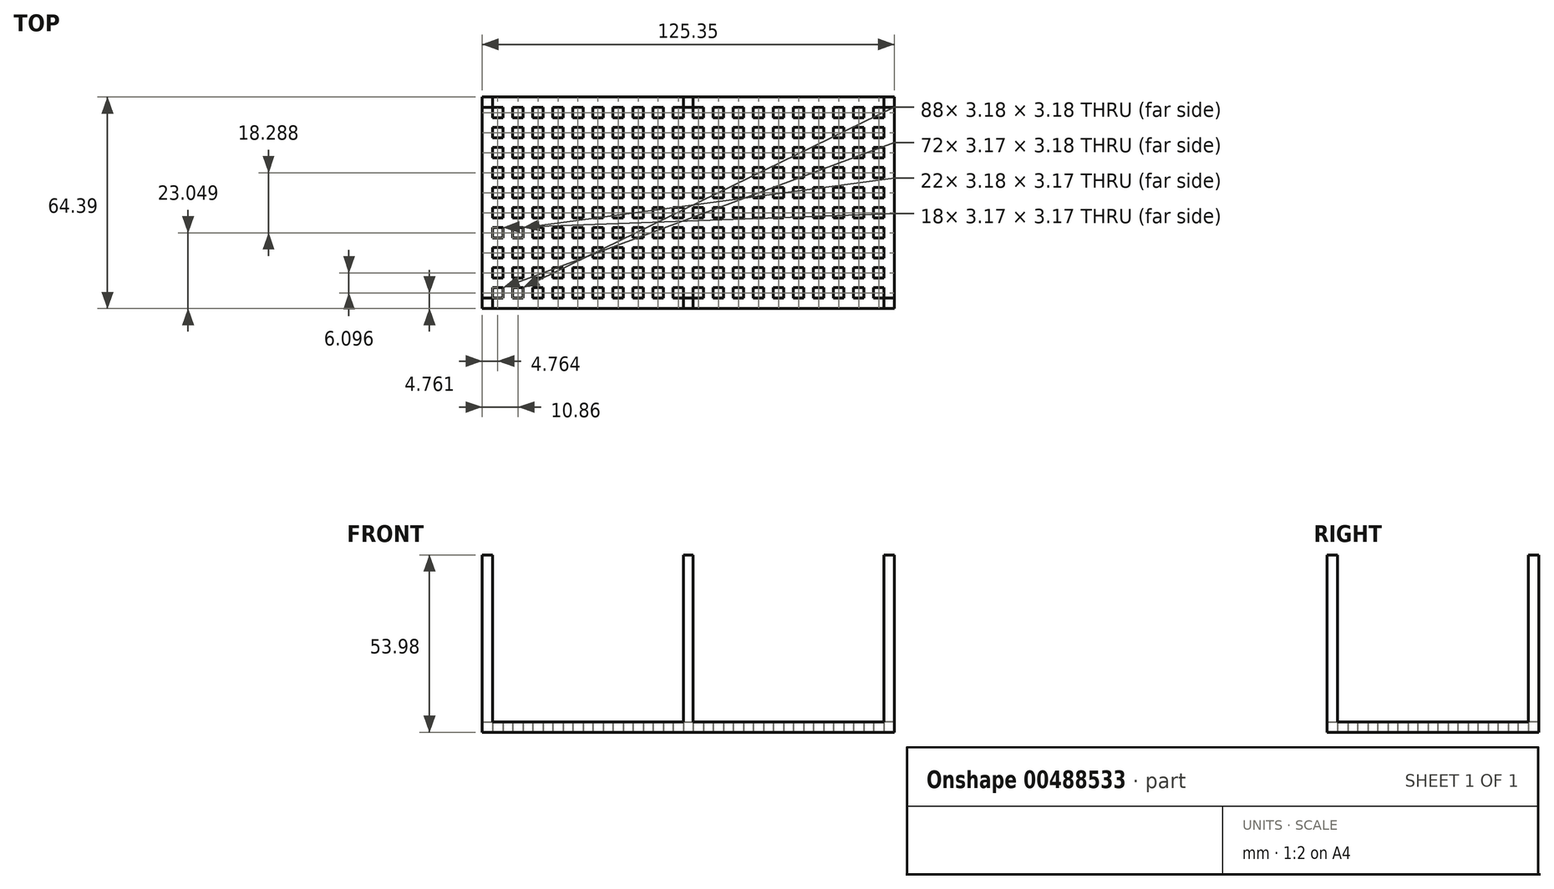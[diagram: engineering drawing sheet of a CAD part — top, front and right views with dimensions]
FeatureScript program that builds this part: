
annotation { "Feature Type Name" : "Feature", "Feature Type Description" : "" }
export const myFeature = defineFeature(function(context is Context, id is Id, definition is map)
    precondition{}
    {
        {
            var Q0;
            Q0=qCreatedBy(makeId("Top.planeOp"),FACE);
            var sketch = newSketch(context, id + "F0", { "sketchPlane" : qUnion([Q0])});
            skLineSegment(sketch, "E0.bottom", {"start": v(-61.85, 33.34) * mm, "end": v(63.5, 33.34) * mm});
            skLineSegment(sketch, "E0.top", {"start": v(-61.85, -31.05) * mm, "end": v(63.5, -31.05) * mm});
            skLineSegment(sketch, "E0.left", {"start": v(-61.85, 33.34) * mm, "end": v(-61.85, -31.05) * mm});
            skLineSegment(sketch, "E0.right", {"start": v(63.5, 33.34) * mm, "end": v(63.5, -31.05) * mm});
            skLineSegment(sketch, "E1.bottom", {"start": v(-58.67, 30.16) * mm, "end": v(-55.5, 30.16) * mm});
            skLineSegment(sketch, "E1.top", {"start": v(-58.67, 26.99) * mm, "end": v(-55.5, 26.99) * mm});
            skLineSegment(sketch, "E1.left", {"start": v(-58.67, 30.16) * mm, "end": v(-58.67, 26.99) * mm});
            skLineSegment(sketch, "E1.right", {"start": v(-55.5, 30.16) * mm, "end": v(-55.5, 26.99) * mm});
            skLineSegment(sketch, "E2.1.0.0", {"start": v(-52.58, 30.16) * mm, "end": v(-49.4, 30.16) * mm});
            skLineSegment(sketch, "E2.1.0.1", {"start": v(-52.58, 30.16) * mm, "end": v(-52.58, 26.99) * mm});
            skLineSegment(sketch, "E2.1.0.2", {"start": v(-52.58, 26.99) * mm, "end": v(-49.4, 26.99) * mm});
            skLineSegment(sketch, "E2.1.0.3", {"start": v(-49.4, 30.16) * mm, "end": v(-49.4, 26.99) * mm});
            skLineSegment(sketch, "E2.2.0.0", {"start": v(-46.48, 30.16) * mm, "end": v(-43.3, 30.16) * mm});
            skLineSegment(sketch, "E2.2.0.1", {"start": v(-46.48, 30.16) * mm, "end": v(-46.48, 26.99) * mm});
            skLineSegment(sketch, "E2.2.0.2", {"start": v(-46.48, 26.99) * mm, "end": v(-43.3, 26.99) * mm});
            skLineSegment(sketch, "E2.2.0.3", {"start": v(-43.3, 30.16) * mm, "end": v(-43.3, 26.99) * mm});
            skLineSegment(sketch, "E2.3.0.0", {"start": v(-40.39, 30.16) * mm, "end": v(-37.21, 30.16) * mm});
            skLineSegment(sketch, "E2.3.0.1", {"start": v(-40.39, 30.16) * mm, "end": v(-40.39, 26.99) * mm});
            skLineSegment(sketch, "E2.3.0.2", {"start": v(-40.39, 26.99) * mm, "end": v(-37.21, 26.99) * mm});
            skLineSegment(sketch, "E2.3.0.3", {"start": v(-37.21, 30.16) * mm, "end": v(-37.21, 26.99) * mm});
            skLineSegment(sketch, "E2.4.0.0", {"start": v(-34.29, 30.16) * mm, "end": v(-31.11, 30.16) * mm});
            skLineSegment(sketch, "E2.4.0.1", {"start": v(-34.29, 30.16) * mm, "end": v(-34.29, 26.99) * mm});
            skLineSegment(sketch, "E2.4.0.2", {"start": v(-34.29, 26.99) * mm, "end": v(-31.11, 26.99) * mm});
            skLineSegment(sketch, "E2.4.0.3", {"start": v(-31.11, 30.16) * mm, "end": v(-31.11, 26.99) * mm});
            skLineSegment(sketch, "E2.direction1", {"start": v(-58.67, 30.16) * mm, "end": v(-52.58, 30.16) * mm, "construction": true});
            skLineSegment(sketch, "E3.0.5.0", {"start": v(-28.2, 30.16) * mm, "end": v(-25.02, 30.16) * mm});
            skLineSegment(sketch, "E3.3.5.0", {"start": v(-28.2, 30.16) * mm, "end": v(-28.2, 26.99) * mm});
            skLineSegment(sketch, "E3.6.5.0", {"start": v(-28.2, 26.99) * mm, "end": v(-25.02, 26.99) * mm});
            skLineSegment(sketch, "E3.9.5.0", {"start": v(-25.02, 30.16) * mm, "end": v(-25.02, 26.99) * mm});
            skLineSegment(sketch, "E3.0.6.0", {"start": v(-22.1, 30.16) * mm, "end": v(-18.92, 30.16) * mm});
            skLineSegment(sketch, "E3.3.6.0", {"start": v(-22.1, 30.16) * mm, "end": v(-22.1, 26.99) * mm});
            skLineSegment(sketch, "E3.6.6.0", {"start": v(-22.1, 26.99) * mm, "end": v(-18.92, 26.99) * mm});
            skLineSegment(sketch, "E3.9.6.0", {"start": v(-18.92, 30.16) * mm, "end": v(-18.92, 26.99) * mm});
            skLineSegment(sketch, "E3.0.7.0", {"start": v(-16, 30.16) * mm, "end": v(-12.83, 30.16) * mm});
            skLineSegment(sketch, "E3.3.7.0", {"start": v(-16, 30.16) * mm, "end": v(-16, 26.99) * mm});
            skLineSegment(sketch, "E3.6.7.0", {"start": v(-16, 26.99) * mm, "end": v(-12.83, 26.99) * mm});
            skLineSegment(sketch, "E3.9.7.0", {"start": v(-12.83, 30.16) * mm, "end": v(-12.83, 26.99) * mm});
            skLineSegment(sketch, "E3.0.8.0", {"start": v(-9.9, 30.16) * mm, "end": v(-6.73, 30.16) * mm});
            skLineSegment(sketch, "E3.3.8.0", {"start": v(-9.9, 30.16) * mm, "end": v(-9.9, 26.99) * mm});
            skLineSegment(sketch, "E3.6.8.0", {"start": v(-9.9, 26.99) * mm, "end": v(-6.73, 26.99) * mm});
            skLineSegment(sketch, "E3.9.8.0", {"start": v(-6.73, 30.16) * mm, "end": v(-6.73, 26.99) * mm});
            skLineSegment(sketch, "E3.0.9.0", {"start": v(-3.8, 30.16) * mm, "end": v(-0.63, 30.16) * mm});
            skLineSegment(sketch, "E3.3.9.0", {"start": v(-3.8, 30.16) * mm, "end": v(-3.8, 26.99) * mm});
            skLineSegment(sketch, "E3.6.9.0", {"start": v(-3.8, 26.99) * mm, "end": v(-0.63, 26.99) * mm});
            skLineSegment(sketch, "E3.9.9.0", {"start": v(-0.63, 30.16) * mm, "end": v(-0.63, 26.99) * mm});
            skLineSegment(sketch, "E4.0.10.0", {"start": v(2.29, 30.16) * mm, "end": v(5.46, 30.16) * mm});
            skLineSegment(sketch, "E4.3.10.0", {"start": v(2.29, 30.16) * mm, "end": v(2.29, 26.99) * mm});
            skLineSegment(sketch, "E4.6.10.0", {"start": v(2.29, 26.99) * mm, "end": v(5.46, 26.99) * mm});
            skLineSegment(sketch, "E4.9.10.0", {"start": v(5.46, 30.16) * mm, "end": v(5.46, 26.99) * mm});
            skLineSegment(sketch, "E4.0.11.0", {"start": v(8.38, 30.16) * mm, "end": v(11.56, 30.16) * mm});
            skLineSegment(sketch, "E4.3.11.0", {"start": v(8.38, 30.16) * mm, "end": v(8.38, 26.99) * mm});
            skLineSegment(sketch, "E4.6.11.0", {"start": v(8.38, 26.99) * mm, "end": v(11.56, 26.99) * mm});
            skLineSegment(sketch, "E4.9.11.0", {"start": v(11.56, 30.16) * mm, "end": v(11.56, 26.99) * mm});
            skLineSegment(sketch, "E4.0.12.0", {"start": v(14.48, 30.16) * mm, "end": v(17.65, 30.16) * mm});
            skLineSegment(sketch, "E4.3.12.0", {"start": v(14.48, 30.16) * mm, "end": v(14.48, 26.99) * mm});
            skLineSegment(sketch, "E4.6.12.0", {"start": v(14.48, 26.99) * mm, "end": v(17.65, 26.99) * mm});
            skLineSegment(sketch, "E4.9.12.0", {"start": v(17.65, 30.16) * mm, "end": v(17.65, 26.99) * mm});
            skLineSegment(sketch, "E4.0.13.0", {"start": v(20.57, 30.16) * mm, "end": v(23.75, 30.16) * mm});
            skLineSegment(sketch, "E4.3.13.0", {"start": v(20.57, 30.16) * mm, "end": v(20.57, 26.99) * mm});
            skLineSegment(sketch, "E4.6.13.0", {"start": v(20.57, 26.99) * mm, "end": v(23.75, 26.99) * mm});
            skLineSegment(sketch, "E4.9.13.0", {"start": v(23.75, 30.16) * mm, "end": v(23.75, 26.99) * mm});
            skLineSegment(sketch, "E4.0.14.0", {"start": v(26.67, 30.16) * mm, "end": v(29.84, 30.16) * mm});
            skLineSegment(sketch, "E4.3.14.0", {"start": v(26.67, 30.16) * mm, "end": v(26.67, 26.99) * mm});
            skLineSegment(sketch, "E4.6.14.0", {"start": v(26.67, 26.99) * mm, "end": v(29.84, 26.99) * mm});
            skLineSegment(sketch, "E4.9.14.0", {"start": v(29.84, 30.16) * mm, "end": v(29.84, 26.99) * mm});
            skLineSegment(sketch, "E4.0.15.0", {"start": v(32.77, 30.16) * mm, "end": v(35.94, 30.16) * mm});
            skLineSegment(sketch, "E4.3.15.0", {"start": v(32.77, 30.16) * mm, "end": v(32.77, 26.99) * mm});
            skLineSegment(sketch, "E4.6.15.0", {"start": v(32.77, 26.99) * mm, "end": v(35.94, 26.99) * mm});
            skLineSegment(sketch, "E4.9.15.0", {"start": v(35.94, 30.16) * mm, "end": v(35.94, 26.99) * mm});
            skLineSegment(sketch, "E4.0.16.0", {"start": v(38.86, 30.16) * mm, "end": v(42.04, 30.16) * mm});
            skLineSegment(sketch, "E4.3.16.0", {"start": v(38.86, 30.16) * mm, "end": v(38.86, 26.99) * mm});
            skLineSegment(sketch, "E4.6.16.0", {"start": v(38.86, 26.99) * mm, "end": v(42.04, 26.99) * mm});
            skLineSegment(sketch, "E4.9.16.0", {"start": v(42.04, 30.16) * mm, "end": v(42.04, 26.99) * mm});
            skLineSegment(sketch, "E4.0.17.0", {"start": v(44.96, 30.16) * mm, "end": v(48.13, 30.16) * mm});
            skLineSegment(sketch, "E4.3.17.0", {"start": v(44.96, 30.16) * mm, "end": v(44.96, 26.99) * mm});
            skLineSegment(sketch, "E4.6.17.0", {"start": v(44.96, 26.99) * mm, "end": v(48.13, 26.99) * mm});
            skLineSegment(sketch, "E4.9.17.0", {"start": v(48.13, 30.16) * mm, "end": v(48.13, 26.99) * mm});
            skLineSegment(sketch, "E4.0.18.0", {"start": v(51.05, 30.16) * mm, "end": v(54.23, 30.16) * mm});
            skLineSegment(sketch, "E4.3.18.0", {"start": v(51.05, 30.16) * mm, "end": v(51.05, 26.99) * mm});
            skLineSegment(sketch, "E4.6.18.0", {"start": v(51.05, 26.99) * mm, "end": v(54.23, 26.99) * mm});
            skLineSegment(sketch, "E4.9.18.0", {"start": v(54.23, 30.16) * mm, "end": v(54.23, 26.99) * mm});
            skLineSegment(sketch, "E4.0.19.0", {"start": v(57.15, 30.16) * mm, "end": v(60.32, 30.16) * mm});
            skLineSegment(sketch, "E4.3.19.0", {"start": v(57.15, 30.16) * mm, "end": v(57.15, 26.99) * mm});
            skLineSegment(sketch, "E4.6.19.0", {"start": v(57.15, 26.99) * mm, "end": v(60.32, 26.99) * mm});
            skLineSegment(sketch, "E4.9.19.0", {"start": v(60.32, 30.16) * mm, "end": v(60.32, 26.99) * mm});
            skLineSegment(sketch, "E5.0.1.0", {"start": v(48.13, 24.07) * mm, "end": v(48.13, 20.9) * mm});
            skLineSegment(sketch, "E5.0.1.1", {"start": v(23.75, 24.07) * mm, "end": v(23.75, 20.9) * mm});
            skLineSegment(sketch, "E5.0.1.2", {"start": v(-0.63, 24.07) * mm, "end": v(-0.63, 20.9) * mm});
            skLineSegment(sketch, "E5.0.1.3", {"start": v(-25.02, 24.07) * mm, "end": v(-25.02, 20.9) * mm});
            skLineSegment(sketch, "E5.0.1.4", {"start": v(51.05, 24.07) * mm, "end": v(54.23, 24.07) * mm});
            skLineSegment(sketch, "E5.0.1.5", {"start": v(26.67, 24.07) * mm, "end": v(29.84, 24.07) * mm});
            skLineSegment(sketch, "E5.0.1.6", {"start": v(2.29, 24.07) * mm, "end": v(5.46, 24.07) * mm});
            skLineSegment(sketch, "E5.0.1.7", {"start": v(-22.1, 24.07) * mm, "end": v(-18.92, 24.07) * mm});
            skLineSegment(sketch, "E5.0.1.8", {"start": v(51.05, 24.07) * mm, "end": v(51.05, 20.9) * mm});
            skLineSegment(sketch, "E5.0.1.9", {"start": v(26.67, 24.07) * mm, "end": v(26.67, 20.9) * mm});
            skLineSegment(sketch, "E5.0.1.10", {"start": v(2.29, 24.07) * mm, "end": v(2.29, 20.9) * mm});
            skLineSegment(sketch, "E5.0.1.11", {"start": v(-22.1, 24.07) * mm, "end": v(-22.1, 20.9) * mm});
            skLineSegment(sketch, "E5.0.1.12", {"start": v(-43.3, 24.07) * mm, "end": v(-43.3, 20.9) * mm});
            skLineSegment(sketch, "E5.0.1.13", {"start": v(51.05, 20.9) * mm, "end": v(54.23, 20.9) * mm});
            skLineSegment(sketch, "E5.0.1.14", {"start": v(26.67, 20.9) * mm, "end": v(29.84, 20.9) * mm});
            skLineSegment(sketch, "E5.0.1.15", {"start": v(2.29, 20.9) * mm, "end": v(5.46, 20.9) * mm});
            skLineSegment(sketch, "E5.0.1.16", {"start": v(-22.1, 20.9) * mm, "end": v(-18.92, 20.9) * mm});
            skLineSegment(sketch, "E5.0.1.17", {"start": v(-40.39, 24.07) * mm, "end": v(-37.21, 24.07) * mm});
            skLineSegment(sketch, "E5.0.1.18", {"start": v(54.23, 24.07) * mm, "end": v(54.23, 20.9) * mm});
            skLineSegment(sketch, "E5.0.1.19", {"start": v(29.84, 24.07) * mm, "end": v(29.84, 20.9) * mm});
            skLineSegment(sketch, "E5.0.1.20", {"start": v(5.46, 24.07) * mm, "end": v(5.46, 20.9) * mm});
            skLineSegment(sketch, "E5.0.1.21", {"start": v(-18.92, 24.07) * mm, "end": v(-18.92, 20.9) * mm});
            skLineSegment(sketch, "E5.0.1.22", {"start": v(-40.39, 24.07) * mm, "end": v(-40.39, 20.9) * mm});
            skLineSegment(sketch, "E5.0.1.23", {"start": v(57.15, 24.07) * mm, "end": v(60.32, 24.07) * mm});
            skLineSegment(sketch, "E5.0.1.24", {"start": v(32.77, 24.07) * mm, "end": v(35.94, 24.07) * mm});
            skLineSegment(sketch, "E5.0.1.25", {"start": v(8.38, 24.07) * mm, "end": v(11.56, 24.07) * mm});
            skLineSegment(sketch, "E5.0.1.26", {"start": v(-16, 24.07) * mm, "end": v(-12.83, 24.07) * mm});
            skLineSegment(sketch, "E5.0.1.27", {"start": v(-40.39, 20.9) * mm, "end": v(-37.21, 20.9) * mm});
            skLineSegment(sketch, "E5.0.1.28", {"start": v(57.15, 24.07) * mm, "end": v(57.15, 20.9) * mm});
            skLineSegment(sketch, "E5.0.1.29", {"start": v(32.77, 24.07) * mm, "end": v(32.77, 20.9) * mm});
            skLineSegment(sketch, "E5.0.1.30", {"start": v(8.38, 24.07) * mm, "end": v(8.38, 20.9) * mm});
            skLineSegment(sketch, "E5.0.1.31", {"start": v(-16, 24.07) * mm, "end": v(-16, 20.9) * mm});
            skLineSegment(sketch, "E5.0.1.32", {"start": v(-37.21, 24.07) * mm, "end": v(-37.21, 20.9) * mm});
            skLineSegment(sketch, "E5.0.1.33", {"start": v(57.15, 20.9) * mm, "end": v(60.32, 20.9) * mm});
            skLineSegment(sketch, "E5.0.1.34", {"start": v(32.77, 20.9) * mm, "end": v(35.94, 20.9) * mm});
            skLineSegment(sketch, "E5.0.1.35", {"start": v(8.38, 20.9) * mm, "end": v(11.56, 20.9) * mm});
            skLineSegment(sketch, "E5.0.1.36", {"start": v(-16, 20.9) * mm, "end": v(-12.83, 20.9) * mm});
            skLineSegment(sketch, "E5.0.1.37", {"start": v(-34.29, 24.07) * mm, "end": v(-31.11, 24.07) * mm});
            skLineSegment(sketch, "E5.0.1.38", {"start": v(60.32, 24.07) * mm, "end": v(60.32, 20.9) * mm});
            skLineSegment(sketch, "E5.0.1.39", {"start": v(35.94, 24.07) * mm, "end": v(35.94, 20.9) * mm});
            skLineSegment(sketch, "E5.0.1.40", {"start": v(11.56, 24.07) * mm, "end": v(11.56, 20.9) * mm});
            skLineSegment(sketch, "E5.0.1.41", {"start": v(-12.83, 24.07) * mm, "end": v(-12.83, 20.9) * mm});
            skLineSegment(sketch, "E5.0.1.42", {"start": v(-34.29, 24.07) * mm, "end": v(-34.29, 20.9) * mm});
            skLineSegment(sketch, "E5.0.1.43", {"start": v(38.86, 24.07) * mm, "end": v(42.04, 24.07) * mm});
            skLineSegment(sketch, "E5.0.1.44", {"start": v(14.48, 24.07) * mm, "end": v(17.65, 24.07) * mm});
            skLineSegment(sketch, "E5.0.1.45", {"start": v(-9.9, 24.07) * mm, "end": v(-6.73, 24.07) * mm});
            skLineSegment(sketch, "E5.0.1.46", {"start": v(14.48, 24.07) * mm, "end": v(14.48, 20.9) * mm});
            skLineSegment(sketch, "E5.0.1.47", {"start": v(-9.9, 24.07) * mm, "end": v(-9.9, 20.9) * mm});
            skLineSegment(sketch, "E5.0.1.48", {"start": v(-34.29, 20.9) * mm, "end": v(-31.11, 20.9) * mm});
            skLineSegment(sketch, "E5.0.1.49", {"start": v(38.86, 24.07) * mm, "end": v(38.86, 20.9) * mm});
            skLineSegment(sketch, "E5.0.1.50", {"start": v(14.48, 20.9) * mm, "end": v(17.65, 20.9) * mm});
            skLineSegment(sketch, "E5.0.1.51", {"start": v(-9.9, 20.9) * mm, "end": v(-6.73, 20.9) * mm});
            skLineSegment(sketch, "E5.0.1.52", {"start": v(-31.11, 24.07) * mm, "end": v(-31.11, 20.9) * mm});
            skLineSegment(sketch, "E5.0.1.53", {"start": v(38.86, 20.9) * mm, "end": v(42.04, 20.9) * mm});
            skLineSegment(sketch, "E5.0.1.54", {"start": v(17.65, 24.07) * mm, "end": v(17.65, 20.9) * mm});
            skLineSegment(sketch, "E5.0.1.55", {"start": v(-6.73, 24.07) * mm, "end": v(-6.73, 20.9) * mm});
            skLineSegment(sketch, "E5.0.1.56", {"start": v(-58.67, 24.07) * mm, "end": v(-52.58, 24.07) * mm, "construction": true});
            skLineSegment(sketch, "E5.0.1.57", {"start": v(42.04, 24.07) * mm, "end": v(42.04, 20.9) * mm});
            skLineSegment(sketch, "E5.0.1.58", {"start": v(20.57, 24.07) * mm, "end": v(23.75, 24.07) * mm});
            skLineSegment(sketch, "E5.0.1.59", {"start": v(-3.8, 24.07) * mm, "end": v(-0.63, 24.07) * mm});
            skLineSegment(sketch, "E5.0.1.60", {"start": v(-28.2, 24.07) * mm, "end": v(-25.02, 24.07) * mm});
            skLineSegment(sketch, "E5.0.1.61", {"start": v(44.96, 24.07) * mm, "end": v(48.13, 24.07) * mm});
            skLineSegment(sketch, "E5.0.1.62", {"start": v(20.57, 24.07) * mm, "end": v(20.57, 20.9) * mm});
            skLineSegment(sketch, "E5.0.1.63", {"start": v(-3.8, 24.07) * mm, "end": v(-3.8, 20.9) * mm});
            skLineSegment(sketch, "E5.0.1.64", {"start": v(-28.2, 24.07) * mm, "end": v(-28.2, 20.9) * mm});
            skLineSegment(sketch, "E5.0.1.65", {"start": v(44.96, 24.07) * mm, "end": v(44.96, 20.9) * mm});
            skLineSegment(sketch, "E5.0.1.66", {"start": v(20.57, 20.9) * mm, "end": v(23.75, 20.9) * mm});
            skLineSegment(sketch, "E5.0.1.67", {"start": v(-3.8, 20.9) * mm, "end": v(-0.63, 20.9) * mm});
            skLineSegment(sketch, "E5.0.1.68", {"start": v(-28.2, 20.9) * mm, "end": v(-25.02, 20.9) * mm});
            skLineSegment(sketch, "E5.0.1.69", {"start": v(44.96, 20.9) * mm, "end": v(48.13, 20.9) * mm});
            skLineSegment(sketch, "E5.0.1.70", {"start": v(-46.48, 24.07) * mm, "end": v(-43.3, 24.07) * mm});
            skLineSegment(sketch, "E5.0.1.71", {"start": v(-46.48, 24.07) * mm, "end": v(-46.48, 20.9) * mm});
            skLineSegment(sketch, "E5.0.1.72", {"start": v(-46.48, 20.9) * mm, "end": v(-43.3, 20.9) * mm});
            skLineSegment(sketch, "E5.0.1.73", {"start": v(-58.67, 20.9) * mm, "end": v(-55.5, 20.9) * mm});
            skLineSegment(sketch, "E5.0.1.74", {"start": v(-58.67, 24.07) * mm, "end": v(-58.67, 20.9) * mm});
            skLineSegment(sketch, "E5.0.1.75", {"start": v(-55.5, 24.07) * mm, "end": v(-55.5, 20.9) * mm});
            skLineSegment(sketch, "E5.0.1.76", {"start": v(-52.58, 24.07) * mm, "end": v(-49.4, 24.07) * mm});
            skLineSegment(sketch, "E5.0.1.77", {"start": v(-52.58, 24.07) * mm, "end": v(-52.58, 20.9) * mm});
            skLineSegment(sketch, "E5.0.1.78", {"start": v(-52.58, 20.9) * mm, "end": v(-49.4, 20.9) * mm});
            skLineSegment(sketch, "E5.0.1.79", {"start": v(-49.4, 24.07) * mm, "end": v(-49.4, 20.9) * mm});
            skLineSegment(sketch, "E5.0.1.80", {"start": v(-58.67, 24.07) * mm, "end": v(-55.5, 24.07) * mm});
            skLineSegment(sketch, "E5.0.2.0", {"start": v(48.13, 17.97) * mm, "end": v(48.13, 14.8) * mm});
            skLineSegment(sketch, "E5.0.2.1", {"start": v(23.75, 17.97) * mm, "end": v(23.75, 14.8) * mm});
            skLineSegment(sketch, "E5.0.2.2", {"start": v(-0.63, 17.97) * mm, "end": v(-0.63, 14.8) * mm});
            skLineSegment(sketch, "E5.0.2.3", {"start": v(-25.02, 17.97) * mm, "end": v(-25.02, 14.8) * mm});
            skLineSegment(sketch, "E5.0.2.4", {"start": v(51.05, 17.97) * mm, "end": v(54.23, 17.97) * mm});
            skLineSegment(sketch, "E5.0.2.5", {"start": v(26.67, 17.97) * mm, "end": v(29.84, 17.97) * mm});
            skLineSegment(sketch, "E5.0.2.6", {"start": v(2.29, 17.97) * mm, "end": v(5.46, 17.97) * mm});
            skLineSegment(sketch, "E5.0.2.7", {"start": v(-22.1, 17.97) * mm, "end": v(-18.92, 17.97) * mm});
            skLineSegment(sketch, "E5.0.2.8", {"start": v(51.05, 17.97) * mm, "end": v(51.05, 14.8) * mm});
            skLineSegment(sketch, "E5.0.2.9", {"start": v(26.67, 17.97) * mm, "end": v(26.67, 14.8) * mm});
            skLineSegment(sketch, "E5.0.2.10", {"start": v(2.29, 17.97) * mm, "end": v(2.29, 14.8) * mm});
            skLineSegment(sketch, "E5.0.2.11", {"start": v(-22.1, 17.97) * mm, "end": v(-22.1, 14.8) * mm});
            skLineSegment(sketch, "E5.0.2.12", {"start": v(-43.3, 17.97) * mm, "end": v(-43.3, 14.8) * mm});
            skLineSegment(sketch, "E5.0.2.13", {"start": v(51.05, 14.8) * mm, "end": v(54.23, 14.8) * mm});
            skLineSegment(sketch, "E5.0.2.14", {"start": v(26.67, 14.8) * mm, "end": v(29.84, 14.8) * mm});
            skLineSegment(sketch, "E5.0.2.15", {"start": v(2.29, 14.8) * mm, "end": v(5.46, 14.8) * mm});
            skLineSegment(sketch, "E5.0.2.16", {"start": v(-22.1, 14.8) * mm, "end": v(-18.92, 14.8) * mm});
            skLineSegment(sketch, "E5.0.2.17", {"start": v(-40.39, 17.97) * mm, "end": v(-37.21, 17.97) * mm});
            skLineSegment(sketch, "E5.0.2.18", {"start": v(54.23, 17.97) * mm, "end": v(54.23, 14.8) * mm});
            skLineSegment(sketch, "E5.0.2.19", {"start": v(29.84, 17.97) * mm, "end": v(29.84, 14.8) * mm});
            skLineSegment(sketch, "E5.0.2.20", {"start": v(5.46, 17.97) * mm, "end": v(5.46, 14.8) * mm});
            skLineSegment(sketch, "E5.0.2.21", {"start": v(-18.92, 17.97) * mm, "end": v(-18.92, 14.8) * mm});
            skLineSegment(sketch, "E5.0.2.22", {"start": v(-40.39, 17.97) * mm, "end": v(-40.39, 14.8) * mm});
            skLineSegment(sketch, "E5.0.2.23", {"start": v(57.15, 17.97) * mm, "end": v(60.32, 17.97) * mm});
            skLineSegment(sketch, "E5.0.2.24", {"start": v(32.77, 17.97) * mm, "end": v(35.94, 17.97) * mm});
            skLineSegment(sketch, "E5.0.2.25", {"start": v(8.38, 17.97) * mm, "end": v(11.56, 17.97) * mm});
            skLineSegment(sketch, "E5.0.2.26", {"start": v(-16, 17.97) * mm, "end": v(-12.83, 17.97) * mm});
            skLineSegment(sketch, "E5.0.2.27", {"start": v(-40.39, 14.8) * mm, "end": v(-37.21, 14.8) * mm});
            skLineSegment(sketch, "E5.0.2.28", {"start": v(57.15, 17.97) * mm, "end": v(57.15, 14.8) * mm});
            skLineSegment(sketch, "E5.0.2.29", {"start": v(32.77, 17.97) * mm, "end": v(32.77, 14.8) * mm});
            skLineSegment(sketch, "E5.0.2.30", {"start": v(8.38, 17.97) * mm, "end": v(8.38, 14.8) * mm});
            skLineSegment(sketch, "E5.0.2.31", {"start": v(-16, 17.97) * mm, "end": v(-16, 14.8) * mm});
            skLineSegment(sketch, "E5.0.2.32", {"start": v(-37.21, 17.97) * mm, "end": v(-37.21, 14.8) * mm});
            skLineSegment(sketch, "E5.0.2.33", {"start": v(57.15, 14.8) * mm, "end": v(60.32, 14.8) * mm});
            skLineSegment(sketch, "E5.0.2.34", {"start": v(32.77, 14.8) * mm, "end": v(35.94, 14.8) * mm});
            skLineSegment(sketch, "E5.0.2.35", {"start": v(8.38, 14.8) * mm, "end": v(11.56, 14.8) * mm});
            skLineSegment(sketch, "E5.0.2.36", {"start": v(-16, 14.8) * mm, "end": v(-12.83, 14.8) * mm});
            skLineSegment(sketch, "E5.0.2.37", {"start": v(-34.29, 17.97) * mm, "end": v(-31.11, 17.97) * mm});
            skLineSegment(sketch, "E5.0.2.38", {"start": v(60.32, 17.97) * mm, "end": v(60.32, 14.8) * mm});
            skLineSegment(sketch, "E5.0.2.39", {"start": v(35.94, 17.97) * mm, "end": v(35.94, 14.8) * mm});
            skLineSegment(sketch, "E5.0.2.40", {"start": v(11.56, 17.97) * mm, "end": v(11.56, 14.8) * mm});
            skLineSegment(sketch, "E5.0.2.41", {"start": v(-12.83, 17.97) * mm, "end": v(-12.83, 14.8) * mm});
            skLineSegment(sketch, "E5.0.2.42", {"start": v(-34.29, 17.97) * mm, "end": v(-34.29, 14.8) * mm});
            skLineSegment(sketch, "E5.0.2.43", {"start": v(38.86, 17.97) * mm, "end": v(42.04, 17.97) * mm});
            skLineSegment(sketch, "E5.0.2.44", {"start": v(14.48, 17.97) * mm, "end": v(17.65, 17.97) * mm});
            skLineSegment(sketch, "E5.0.2.45", {"start": v(-9.9, 17.97) * mm, "end": v(-6.73, 17.97) * mm});
            skLineSegment(sketch, "E5.0.2.46", {"start": v(14.48, 17.97) * mm, "end": v(14.48, 14.8) * mm});
            skLineSegment(sketch, "E5.0.2.47", {"start": v(-9.9, 17.97) * mm, "end": v(-9.9, 14.8) * mm});
            skLineSegment(sketch, "E5.0.2.48", {"start": v(-34.29, 14.8) * mm, "end": v(-31.11, 14.8) * mm});
            skLineSegment(sketch, "E5.0.2.49", {"start": v(38.86, 17.97) * mm, "end": v(38.86, 14.8) * mm});
            skLineSegment(sketch, "E5.0.2.50", {"start": v(14.48, 14.8) * mm, "end": v(17.65, 14.8) * mm});
            skLineSegment(sketch, "E5.0.2.51", {"start": v(-9.9, 14.8) * mm, "end": v(-6.73, 14.8) * mm});
            skLineSegment(sketch, "E5.0.2.52", {"start": v(-31.11, 17.97) * mm, "end": v(-31.11, 14.8) * mm});
            skLineSegment(sketch, "E5.0.2.53", {"start": v(38.86, 14.8) * mm, "end": v(42.04, 14.8) * mm});
            skLineSegment(sketch, "E5.0.2.54", {"start": v(17.65, 17.97) * mm, "end": v(17.65, 14.8) * mm});
            skLineSegment(sketch, "E5.0.2.55", {"start": v(-6.73, 17.97) * mm, "end": v(-6.73, 14.8) * mm});
            skLineSegment(sketch, "E5.0.2.56", {"start": v(-58.67, 17.97) * mm, "end": v(-52.58, 17.97) * mm, "construction": true});
            skLineSegment(sketch, "E5.0.2.57", {"start": v(42.04, 17.97) * mm, "end": v(42.04, 14.8) * mm});
            skLineSegment(sketch, "E5.0.2.58", {"start": v(20.57, 17.97) * mm, "end": v(23.75, 17.97) * mm});
            skLineSegment(sketch, "E5.0.2.59", {"start": v(-3.8, 17.97) * mm, "end": v(-0.63, 17.97) * mm});
            skLineSegment(sketch, "E5.0.2.60", {"start": v(-28.2, 17.97) * mm, "end": v(-25.02, 17.97) * mm});
            skLineSegment(sketch, "E5.0.2.61", {"start": v(44.96, 17.97) * mm, "end": v(48.13, 17.97) * mm});
            skLineSegment(sketch, "E5.0.2.62", {"start": v(20.57, 17.97) * mm, "end": v(20.57, 14.8) * mm});
            skLineSegment(sketch, "E5.0.2.63", {"start": v(-3.8, 17.97) * mm, "end": v(-3.8, 14.8) * mm});
            skLineSegment(sketch, "E5.0.2.64", {"start": v(-28.2, 17.97) * mm, "end": v(-28.2, 14.8) * mm});
            skLineSegment(sketch, "E5.0.2.65", {"start": v(44.96, 17.97) * mm, "end": v(44.96, 14.8) * mm});
            skLineSegment(sketch, "E5.0.2.66", {"start": v(20.57, 14.8) * mm, "end": v(23.75, 14.8) * mm});
            skLineSegment(sketch, "E5.0.2.67", {"start": v(-3.8, 14.8) * mm, "end": v(-0.63, 14.8) * mm});
            skLineSegment(sketch, "E5.0.2.68", {"start": v(-28.2, 14.8) * mm, "end": v(-25.02, 14.8) * mm});
            skLineSegment(sketch, "E5.0.2.69", {"start": v(44.96, 14.8) * mm, "end": v(48.13, 14.8) * mm});
            skLineSegment(sketch, "E5.0.2.70", {"start": v(-46.48, 17.97) * mm, "end": v(-43.3, 17.97) * mm});
            skLineSegment(sketch, "E5.0.2.71", {"start": v(-46.48, 17.97) * mm, "end": v(-46.48, 14.8) * mm});
            skLineSegment(sketch, "E5.0.2.72", {"start": v(-46.48, 14.8) * mm, "end": v(-43.3, 14.8) * mm});
            skLineSegment(sketch, "E5.0.2.73", {"start": v(-58.67, 14.8) * mm, "end": v(-55.5, 14.8) * mm});
            skLineSegment(sketch, "E5.0.2.74", {"start": v(-58.67, 17.97) * mm, "end": v(-58.67, 14.8) * mm});
            skLineSegment(sketch, "E5.0.2.75", {"start": v(-55.5, 17.97) * mm, "end": v(-55.5, 14.8) * mm});
            skLineSegment(sketch, "E5.0.2.76", {"start": v(-52.58, 17.97) * mm, "end": v(-49.4, 17.97) * mm});
            skLineSegment(sketch, "E5.0.2.77", {"start": v(-52.58, 17.97) * mm, "end": v(-52.58, 14.8) * mm});
            skLineSegment(sketch, "E5.0.2.78", {"start": v(-52.58, 14.8) * mm, "end": v(-49.4, 14.8) * mm});
            skLineSegment(sketch, "E5.0.2.79", {"start": v(-49.4, 17.97) * mm, "end": v(-49.4, 14.8) * mm});
            skLineSegment(sketch, "E5.0.2.80", {"start": v(-58.67, 17.97) * mm, "end": v(-55.5, 17.97) * mm});
            skLineSegment(sketch, "E5.0.3.0", {"start": v(48.13, 11.87) * mm, "end": v(48.13, 8.7) * mm});
            skLineSegment(sketch, "E5.0.3.1", {"start": v(23.75, 11.87) * mm, "end": v(23.75, 8.7) * mm});
            skLineSegment(sketch, "E5.0.3.2", {"start": v(-0.63, 11.87) * mm, "end": v(-0.63, 8.7) * mm});
            skLineSegment(sketch, "E5.0.3.3", {"start": v(-25.02, 11.87) * mm, "end": v(-25.02, 8.7) * mm});
            skLineSegment(sketch, "E5.0.3.4", {"start": v(51.05, 11.87) * mm, "end": v(54.23, 11.87) * mm});
            skLineSegment(sketch, "E5.0.3.5", {"start": v(26.67, 11.87) * mm, "end": v(29.84, 11.87) * mm});
            skLineSegment(sketch, "E5.0.3.6", {"start": v(2.29, 11.87) * mm, "end": v(5.46, 11.87) * mm});
            skLineSegment(sketch, "E5.0.3.7", {"start": v(-22.1, 11.87) * mm, "end": v(-18.92, 11.87) * mm});
            skLineSegment(sketch, "E5.0.3.8", {"start": v(51.05, 11.87) * mm, "end": v(51.05, 8.7) * mm});
            skLineSegment(sketch, "E5.0.3.9", {"start": v(26.67, 11.87) * mm, "end": v(26.67, 8.7) * mm});
            skLineSegment(sketch, "E5.0.3.10", {"start": v(2.29, 11.87) * mm, "end": v(2.29, 8.7) * mm});
            skLineSegment(sketch, "E5.0.3.11", {"start": v(-22.1, 11.87) * mm, "end": v(-22.1, 8.7) * mm});
            skLineSegment(sketch, "E5.0.3.12", {"start": v(-43.3, 11.87) * mm, "end": v(-43.3, 8.7) * mm});
            skLineSegment(sketch, "E5.0.3.13", {"start": v(51.05, 8.7) * mm, "end": v(54.23, 8.7) * mm});
            skLineSegment(sketch, "E5.0.3.14", {"start": v(26.67, 8.7) * mm, "end": v(29.84, 8.7) * mm});
            skLineSegment(sketch, "E5.0.3.15", {"start": v(2.29, 8.7) * mm, "end": v(5.46, 8.7) * mm});
            skLineSegment(sketch, "E5.0.3.16", {"start": v(-22.1, 8.7) * mm, "end": v(-18.92, 8.7) * mm});
            skLineSegment(sketch, "E5.0.3.17", {"start": v(-40.39, 11.87) * mm, "end": v(-37.21, 11.87) * mm});
            skLineSegment(sketch, "E5.0.3.18", {"start": v(54.23, 11.87) * mm, "end": v(54.23, 8.7) * mm});
            skLineSegment(sketch, "E5.0.3.19", {"start": v(29.84, 11.87) * mm, "end": v(29.84, 8.7) * mm});
            skLineSegment(sketch, "E5.0.3.20", {"start": v(5.46, 11.87) * mm, "end": v(5.46, 8.7) * mm});
            skLineSegment(sketch, "E5.0.3.21", {"start": v(-18.92, 11.87) * mm, "end": v(-18.92, 8.7) * mm});
            skLineSegment(sketch, "E5.0.3.22", {"start": v(-40.39, 11.87) * mm, "end": v(-40.39, 8.7) * mm});
            skLineSegment(sketch, "E5.0.3.23", {"start": v(57.15, 11.87) * mm, "end": v(60.32, 11.87) * mm});
            skLineSegment(sketch, "E5.0.3.24", {"start": v(32.77, 11.87) * mm, "end": v(35.94, 11.87) * mm});
            skLineSegment(sketch, "E5.0.3.25", {"start": v(8.38, 11.87) * mm, "end": v(11.56, 11.87) * mm});
            skLineSegment(sketch, "E5.0.3.26", {"start": v(-16, 11.87) * mm, "end": v(-12.83, 11.87) * mm});
            skLineSegment(sketch, "E5.0.3.27", {"start": v(-40.39, 8.7) * mm, "end": v(-37.21, 8.7) * mm});
            skLineSegment(sketch, "E5.0.3.28", {"start": v(57.15, 11.87) * mm, "end": v(57.15, 8.7) * mm});
            skLineSegment(sketch, "E5.0.3.29", {"start": v(32.77, 11.87) * mm, "end": v(32.77, 8.7) * mm});
            skLineSegment(sketch, "E5.0.3.30", {"start": v(8.38, 11.87) * mm, "end": v(8.38, 8.7) * mm});
            skLineSegment(sketch, "E5.0.3.31", {"start": v(-16, 11.87) * mm, "end": v(-16, 8.7) * mm});
            skLineSegment(sketch, "E5.0.3.32", {"start": v(-37.21, 11.87) * mm, "end": v(-37.21, 8.7) * mm});
            skLineSegment(sketch, "E5.0.3.33", {"start": v(57.15, 8.7) * mm, "end": v(60.32, 8.7) * mm});
            skLineSegment(sketch, "E5.0.3.34", {"start": v(32.77, 8.7) * mm, "end": v(35.94, 8.7) * mm});
            skLineSegment(sketch, "E5.0.3.35", {"start": v(8.38, 8.7) * mm, "end": v(11.56, 8.7) * mm});
            skLineSegment(sketch, "E5.0.3.36", {"start": v(-16, 8.7) * mm, "end": v(-12.83, 8.7) * mm});
            skLineSegment(sketch, "E5.0.3.37", {"start": v(-34.29, 11.87) * mm, "end": v(-31.11, 11.87) * mm});
            skLineSegment(sketch, "E5.0.3.38", {"start": v(60.32, 11.87) * mm, "end": v(60.32, 8.7) * mm});
            skLineSegment(sketch, "E5.0.3.39", {"start": v(35.94, 11.87) * mm, "end": v(35.94, 8.7) * mm});
            skLineSegment(sketch, "E5.0.3.40", {"start": v(11.56, 11.87) * mm, "end": v(11.56, 8.7) * mm});
            skLineSegment(sketch, "E5.0.3.41", {"start": v(-12.83, 11.87) * mm, "end": v(-12.83, 8.7) * mm});
            skLineSegment(sketch, "E5.0.3.42", {"start": v(-34.29, 11.87) * mm, "end": v(-34.29, 8.7) * mm});
            skLineSegment(sketch, "E5.0.3.43", {"start": v(38.86, 11.87) * mm, "end": v(42.04, 11.87) * mm});
            skLineSegment(sketch, "E5.0.3.44", {"start": v(14.48, 11.87) * mm, "end": v(17.65, 11.87) * mm});
            skLineSegment(sketch, "E5.0.3.45", {"start": v(-9.9, 11.87) * mm, "end": v(-6.73, 11.87) * mm});
            skLineSegment(sketch, "E5.0.3.46", {"start": v(14.48, 11.87) * mm, "end": v(14.48, 8.7) * mm});
            skLineSegment(sketch, "E5.0.3.47", {"start": v(-9.9, 11.87) * mm, "end": v(-9.9, 8.7) * mm});
            skLineSegment(sketch, "E5.0.3.48", {"start": v(-34.29, 8.7) * mm, "end": v(-31.11, 8.7) * mm});
            skLineSegment(sketch, "E5.0.3.49", {"start": v(38.86, 11.87) * mm, "end": v(38.86, 8.7) * mm});
            skLineSegment(sketch, "E5.0.3.50", {"start": v(14.48, 8.7) * mm, "end": v(17.65, 8.7) * mm});
            skLineSegment(sketch, "E5.0.3.51", {"start": v(-9.9, 8.7) * mm, "end": v(-6.73, 8.7) * mm});
            skLineSegment(sketch, "E5.0.3.52", {"start": v(-31.11, 11.87) * mm, "end": v(-31.11, 8.7) * mm});
            skLineSegment(sketch, "E5.0.3.53", {"start": v(38.86, 8.7) * mm, "end": v(42.04, 8.7) * mm});
            skLineSegment(sketch, "E5.0.3.54", {"start": v(17.65, 11.87) * mm, "end": v(17.65, 8.7) * mm});
            skLineSegment(sketch, "E5.0.3.55", {"start": v(-6.73, 11.87) * mm, "end": v(-6.73, 8.7) * mm});
            skLineSegment(sketch, "E5.0.3.56", {"start": v(-58.67, 11.87) * mm, "end": v(-52.58, 11.87) * mm, "construction": true});
            skLineSegment(sketch, "E5.0.3.57", {"start": v(42.04, 11.87) * mm, "end": v(42.04, 8.7) * mm});
            skLineSegment(sketch, "E5.0.3.58", {"start": v(20.57, 11.87) * mm, "end": v(23.75, 11.87) * mm});
            skLineSegment(sketch, "E5.0.3.59", {"start": v(-3.8, 11.87) * mm, "end": v(-0.63, 11.87) * mm});
            skLineSegment(sketch, "E5.0.3.60", {"start": v(-28.2, 11.87) * mm, "end": v(-25.02, 11.87) * mm});
            skLineSegment(sketch, "E5.0.3.61", {"start": v(44.96, 11.87) * mm, "end": v(48.13, 11.87) * mm});
            skLineSegment(sketch, "E5.0.3.62", {"start": v(20.57, 11.87) * mm, "end": v(20.57, 8.7) * mm});
            skLineSegment(sketch, "E5.0.3.63", {"start": v(-3.8, 11.87) * mm, "end": v(-3.8, 8.7) * mm});
            skLineSegment(sketch, "E5.0.3.64", {"start": v(-28.2, 11.87) * mm, "end": v(-28.2, 8.7) * mm});
            skLineSegment(sketch, "E5.0.3.65", {"start": v(44.96, 11.87) * mm, "end": v(44.96, 8.7) * mm});
            skLineSegment(sketch, "E5.0.3.66", {"start": v(20.57, 8.7) * mm, "end": v(23.75, 8.7) * mm});
            skLineSegment(sketch, "E5.0.3.67", {"start": v(-3.8, 8.7) * mm, "end": v(-0.63, 8.7) * mm});
            skLineSegment(sketch, "E5.0.3.68", {"start": v(-28.2, 8.7) * mm, "end": v(-25.02, 8.7) * mm});
            skLineSegment(sketch, "E5.0.3.69", {"start": v(44.96, 8.7) * mm, "end": v(48.13, 8.7) * mm});
            skLineSegment(sketch, "E5.0.3.70", {"start": v(-46.48, 11.87) * mm, "end": v(-43.3, 11.87) * mm});
            skLineSegment(sketch, "E5.0.3.71", {"start": v(-46.48, 11.87) * mm, "end": v(-46.48, 8.7) * mm});
            skLineSegment(sketch, "E5.0.3.72", {"start": v(-46.48, 8.7) * mm, "end": v(-43.3, 8.7) * mm});
            skLineSegment(sketch, "E5.0.3.73", {"start": v(-58.67, 8.7) * mm, "end": v(-55.5, 8.7) * mm});
            skLineSegment(sketch, "E5.0.3.74", {"start": v(-58.67, 11.87) * mm, "end": v(-58.67, 8.7) * mm});
            skLineSegment(sketch, "E5.0.3.75", {"start": v(-55.5, 11.87) * mm, "end": v(-55.5, 8.7) * mm});
            skLineSegment(sketch, "E5.0.3.76", {"start": v(-52.58, 11.87) * mm, "end": v(-49.4, 11.87) * mm});
            skLineSegment(sketch, "E5.0.3.77", {"start": v(-52.58, 11.87) * mm, "end": v(-52.58, 8.7) * mm});
            skLineSegment(sketch, "E5.0.3.78", {"start": v(-52.58, 8.7) * mm, "end": v(-49.4, 8.7) * mm});
            skLineSegment(sketch, "E5.0.3.79", {"start": v(-49.4, 11.87) * mm, "end": v(-49.4, 8.7) * mm});
            skLineSegment(sketch, "E5.0.3.80", {"start": v(-58.67, 11.87) * mm, "end": v(-55.5, 11.87) * mm});
            skLineSegment(sketch, "E5.0.4.0", {"start": v(48.13, 5.78) * mm, "end": v(48.13, 2.6) * mm});
            skLineSegment(sketch, "E5.0.4.1", {"start": v(23.75, 5.78) * mm, "end": v(23.75, 2.6) * mm});
            skLineSegment(sketch, "E5.0.4.2", {"start": v(-0.63, 5.78) * mm, "end": v(-0.63, 2.6) * mm});
            skLineSegment(sketch, "E5.0.4.3", {"start": v(-25.02, 5.78) * mm, "end": v(-25.02, 2.6) * mm});
            skLineSegment(sketch, "E5.0.4.4", {"start": v(51.05, 5.78) * mm, "end": v(54.23, 5.78) * mm});
            skLineSegment(sketch, "E5.0.4.5", {"start": v(26.67, 5.78) * mm, "end": v(29.84, 5.78) * mm});
            skLineSegment(sketch, "E5.0.4.6", {"start": v(2.29, 5.78) * mm, "end": v(5.46, 5.78) * mm});
            skLineSegment(sketch, "E5.0.4.7", {"start": v(-22.1, 5.78) * mm, "end": v(-18.92, 5.78) * mm});
            skLineSegment(sketch, "E5.0.4.8", {"start": v(51.05, 5.78) * mm, "end": v(51.05, 2.6) * mm});
            skLineSegment(sketch, "E5.0.4.9", {"start": v(26.67, 5.78) * mm, "end": v(26.67, 2.6) * mm});
            skLineSegment(sketch, "E5.0.4.10", {"start": v(2.29, 5.78) * mm, "end": v(2.29, 2.6) * mm});
            skLineSegment(sketch, "E5.0.4.11", {"start": v(-22.1, 5.78) * mm, "end": v(-22.1, 2.6) * mm});
            skLineSegment(sketch, "E5.0.4.12", {"start": v(-43.3, 5.78) * mm, "end": v(-43.3, 2.6) * mm});
            skLineSegment(sketch, "E5.0.4.13", {"start": v(51.05, 2.6) * mm, "end": v(54.23, 2.6) * mm});
            skLineSegment(sketch, "E5.0.4.14", {"start": v(26.67, 2.6) * mm, "end": v(29.84, 2.6) * mm});
            skLineSegment(sketch, "E5.0.4.15", {"start": v(2.29, 2.6) * mm, "end": v(5.46, 2.6) * mm});
            skLineSegment(sketch, "E5.0.4.16", {"start": v(-22.1, 2.6) * mm, "end": v(-18.92, 2.6) * mm});
            skLineSegment(sketch, "E5.0.4.17", {"start": v(-40.39, 5.78) * mm, "end": v(-37.21, 5.78) * mm});
            skLineSegment(sketch, "E5.0.4.18", {"start": v(54.23, 5.78) * mm, "end": v(54.23, 2.6) * mm});
            skLineSegment(sketch, "E5.0.4.19", {"start": v(29.84, 5.78) * mm, "end": v(29.84, 2.6) * mm});
            skLineSegment(sketch, "E5.0.4.20", {"start": v(5.46, 5.78) * mm, "end": v(5.46, 2.6) * mm});
            skLineSegment(sketch, "E5.0.4.21", {"start": v(-18.92, 5.78) * mm, "end": v(-18.92, 2.6) * mm});
            skLineSegment(sketch, "E5.0.4.22", {"start": v(-40.39, 5.78) * mm, "end": v(-40.39, 2.6) * mm});
            skLineSegment(sketch, "E5.0.4.23", {"start": v(57.15, 5.78) * mm, "end": v(60.32, 5.78) * mm});
            skLineSegment(sketch, "E5.0.4.24", {"start": v(32.77, 5.78) * mm, "end": v(35.94, 5.78) * mm});
            skLineSegment(sketch, "E5.0.4.25", {"start": v(8.38, 5.78) * mm, "end": v(11.56, 5.78) * mm});
            skLineSegment(sketch, "E5.0.4.26", {"start": v(-16, 5.78) * mm, "end": v(-12.83, 5.78) * mm});
            skLineSegment(sketch, "E5.0.4.27", {"start": v(-40.39, 2.6) * mm, "end": v(-37.21, 2.6) * mm});
            skLineSegment(sketch, "E5.0.4.28", {"start": v(57.15, 5.78) * mm, "end": v(57.15, 2.6) * mm});
            skLineSegment(sketch, "E5.0.4.29", {"start": v(32.77, 5.78) * mm, "end": v(32.77, 2.6) * mm});
            skLineSegment(sketch, "E5.0.4.30", {"start": v(8.38, 5.78) * mm, "end": v(8.38, 2.6) * mm});
            skLineSegment(sketch, "E5.0.4.31", {"start": v(-16, 5.78) * mm, "end": v(-16, 2.6) * mm});
            skLineSegment(sketch, "E5.0.4.32", {"start": v(-37.21, 5.78) * mm, "end": v(-37.21, 2.6) * mm});
            skLineSegment(sketch, "E5.0.4.33", {"start": v(57.15, 2.6) * mm, "end": v(60.32, 2.6) * mm});
            skLineSegment(sketch, "E5.0.4.34", {"start": v(32.77, 2.6) * mm, "end": v(35.94, 2.6) * mm});
            skLineSegment(sketch, "E5.0.4.35", {"start": v(8.38, 2.6) * mm, "end": v(11.56, 2.6) * mm});
            skLineSegment(sketch, "E5.0.4.36", {"start": v(-16, 2.6) * mm, "end": v(-12.83, 2.6) * mm});
            skLineSegment(sketch, "E5.0.4.37", {"start": v(-34.29, 5.78) * mm, "end": v(-31.11, 5.78) * mm});
            skLineSegment(sketch, "E5.0.4.38", {"start": v(60.32, 5.78) * mm, "end": v(60.32, 2.6) * mm});
            skLineSegment(sketch, "E5.0.4.39", {"start": v(35.94, 5.78) * mm, "end": v(35.94, 2.6) * mm});
            skLineSegment(sketch, "E5.0.4.40", {"start": v(11.56, 5.78) * mm, "end": v(11.56, 2.6) * mm});
            skLineSegment(sketch, "E5.0.4.41", {"start": v(-12.83, 5.78) * mm, "end": v(-12.83, 2.6) * mm});
            skLineSegment(sketch, "E5.0.4.42", {"start": v(-34.29, 5.78) * mm, "end": v(-34.29, 2.6) * mm});
            skLineSegment(sketch, "E5.0.4.43", {"start": v(38.86, 5.78) * mm, "end": v(42.04, 5.78) * mm});
            skLineSegment(sketch, "E5.0.4.44", {"start": v(14.48, 5.78) * mm, "end": v(17.65, 5.78) * mm});
            skLineSegment(sketch, "E5.0.4.45", {"start": v(-9.9, 5.78) * mm, "end": v(-6.73, 5.78) * mm});
            skLineSegment(sketch, "E5.0.4.46", {"start": v(14.48, 5.78) * mm, "end": v(14.48, 2.6) * mm});
            skLineSegment(sketch, "E5.0.4.47", {"start": v(-9.9, 5.78) * mm, "end": v(-9.9, 2.6) * mm});
            skLineSegment(sketch, "E5.0.4.48", {"start": v(-34.29, 2.6) * mm, "end": v(-31.11, 2.6) * mm});
            skLineSegment(sketch, "E5.0.4.49", {"start": v(38.86, 5.78) * mm, "end": v(38.86, 2.6) * mm});
            skLineSegment(sketch, "E5.0.4.50", {"start": v(14.48, 2.6) * mm, "end": v(17.65, 2.6) * mm});
            skLineSegment(sketch, "E5.0.4.51", {"start": v(-9.9, 2.6) * mm, "end": v(-6.73, 2.6) * mm});
            skLineSegment(sketch, "E5.0.4.52", {"start": v(-31.11, 5.78) * mm, "end": v(-31.11, 2.6) * mm});
            skLineSegment(sketch, "E5.0.4.53", {"start": v(38.86, 2.6) * mm, "end": v(42.04, 2.6) * mm});
            skLineSegment(sketch, "E5.0.4.54", {"start": v(17.65, 5.78) * mm, "end": v(17.65, 2.6) * mm});
            skLineSegment(sketch, "E5.0.4.55", {"start": v(-6.73, 5.78) * mm, "end": v(-6.73, 2.6) * mm});
            skLineSegment(sketch, "E5.0.4.56", {"start": v(-58.67, 5.78) * mm, "end": v(-52.58, 5.78) * mm, "construction": true});
            skLineSegment(sketch, "E5.0.4.57", {"start": v(42.04, 5.78) * mm, "end": v(42.04, 2.6) * mm});
            skLineSegment(sketch, "E5.0.4.58", {"start": v(20.57, 5.78) * mm, "end": v(23.75, 5.78) * mm});
            skLineSegment(sketch, "E5.0.4.59", {"start": v(-3.8, 5.78) * mm, "end": v(-0.63, 5.78) * mm});
            skLineSegment(sketch, "E5.0.4.60", {"start": v(-28.2, 5.78) * mm, "end": v(-25.02, 5.78) * mm});
            skLineSegment(sketch, "E5.0.4.61", {"start": v(44.96, 5.78) * mm, "end": v(48.13, 5.78) * mm});
            skLineSegment(sketch, "E5.0.4.62", {"start": v(20.57, 5.78) * mm, "end": v(20.57, 2.6) * mm});
            skLineSegment(sketch, "E5.0.4.63", {"start": v(-3.8, 5.78) * mm, "end": v(-3.8, 2.6) * mm});
            skLineSegment(sketch, "E5.0.4.64", {"start": v(-28.2, 5.78) * mm, "end": v(-28.2, 2.6) * mm});
            skLineSegment(sketch, "E5.0.4.65", {"start": v(44.96, 5.78) * mm, "end": v(44.96, 2.6) * mm});
            skLineSegment(sketch, "E5.0.4.66", {"start": v(20.57, 2.6) * mm, "end": v(23.75, 2.6) * mm});
            skLineSegment(sketch, "E5.0.4.67", {"start": v(-3.8, 2.6) * mm, "end": v(-0.63, 2.6) * mm});
            skLineSegment(sketch, "E5.0.4.68", {"start": v(-28.2, 2.6) * mm, "end": v(-25.02, 2.6) * mm});
            skLineSegment(sketch, "E5.0.4.69", {"start": v(44.96, 2.6) * mm, "end": v(48.13, 2.6) * mm});
            skLineSegment(sketch, "E5.0.4.70", {"start": v(-46.48, 5.78) * mm, "end": v(-43.3, 5.78) * mm});
            skLineSegment(sketch, "E5.0.4.71", {"start": v(-46.48, 5.78) * mm, "end": v(-46.48, 2.6) * mm});
            skLineSegment(sketch, "E5.0.4.72", {"start": v(-46.48, 2.6) * mm, "end": v(-43.3, 2.6) * mm});
            skLineSegment(sketch, "E5.0.4.73", {"start": v(-58.67, 2.6) * mm, "end": v(-55.5, 2.6) * mm});
            skLineSegment(sketch, "E5.0.4.74", {"start": v(-58.67, 5.78) * mm, "end": v(-58.67, 2.6) * mm});
            skLineSegment(sketch, "E5.0.4.75", {"start": v(-55.5, 5.78) * mm, "end": v(-55.5, 2.6) * mm});
            skLineSegment(sketch, "E5.0.4.76", {"start": v(-52.58, 5.78) * mm, "end": v(-49.4, 5.78) * mm});
            skLineSegment(sketch, "E5.0.4.77", {"start": v(-52.58, 5.78) * mm, "end": v(-52.58, 2.6) * mm});
            skLineSegment(sketch, "E5.0.4.78", {"start": v(-52.58, 2.6) * mm, "end": v(-49.4, 2.6) * mm});
            skLineSegment(sketch, "E5.0.4.79", {"start": v(-49.4, 5.78) * mm, "end": v(-49.4, 2.6) * mm});
            skLineSegment(sketch, "E5.0.4.80", {"start": v(-58.67, 5.78) * mm, "end": v(-55.5, 5.78) * mm});
            skLineSegment(sketch, "E5.0.5.0", {"start": v(48.13, -0.32) * mm, "end": v(48.13, -3.5) * mm});
            skLineSegment(sketch, "E5.0.5.1", {"start": v(23.75, -0.32) * mm, "end": v(23.75, -3.5) * mm});
            skLineSegment(sketch, "E5.0.5.2", {"start": v(-0.63, -0.32) * mm, "end": v(-0.63, -3.5) * mm});
            skLineSegment(sketch, "E5.0.5.3", {"start": v(-25.02, -0.32) * mm, "end": v(-25.02, -3.5) * mm});
            skLineSegment(sketch, "E5.0.5.4", {"start": v(51.05, -0.32) * mm, "end": v(54.23, -0.32) * mm});
            skLineSegment(sketch, "E5.0.5.5", {"start": v(26.67, -0.32) * mm, "end": v(29.84, -0.32) * mm});
            skLineSegment(sketch, "E5.0.5.6", {"start": v(2.29, -0.32) * mm, "end": v(5.46, -0.32) * mm});
            skLineSegment(sketch, "E5.0.5.7", {"start": v(-22.1, -0.32) * mm, "end": v(-18.92, -0.32) * mm});
            skLineSegment(sketch, "E5.0.5.8", {"start": v(51.05, -0.32) * mm, "end": v(51.05, -3.5) * mm});
            skLineSegment(sketch, "E5.0.5.9", {"start": v(26.67, -0.32) * mm, "end": v(26.67, -3.5) * mm});
            skLineSegment(sketch, "E5.0.5.10", {"start": v(2.29, -0.32) * mm, "end": v(2.29, -3.5) * mm});
            skLineSegment(sketch, "E5.0.5.11", {"start": v(-22.1, -0.32) * mm, "end": v(-22.1, -3.5) * mm});
            skLineSegment(sketch, "E5.0.5.12", {"start": v(-43.3, -0.32) * mm, "end": v(-43.3, -3.5) * mm});
            skLineSegment(sketch, "E5.0.5.13", {"start": v(51.05, -3.5) * mm, "end": v(54.23, -3.5) * mm});
            skLineSegment(sketch, "E5.0.5.14", {"start": v(26.67, -3.5) * mm, "end": v(29.84, -3.5) * mm});
            skLineSegment(sketch, "E5.0.5.15", {"start": v(2.29, -3.5) * mm, "end": v(5.46, -3.5) * mm});
            skLineSegment(sketch, "E5.0.5.16", {"start": v(-22.1, -3.5) * mm, "end": v(-18.92, -3.5) * mm});
            skLineSegment(sketch, "E5.0.5.17", {"start": v(-40.39, -0.32) * mm, "end": v(-37.21, -0.32) * mm});
            skLineSegment(sketch, "E5.0.5.18", {"start": v(54.23, -0.32) * mm, "end": v(54.23, -3.5) * mm});
            skLineSegment(sketch, "E5.0.5.19", {"start": v(29.84, -0.32) * mm, "end": v(29.84, -3.5) * mm});
            skLineSegment(sketch, "E5.0.5.20", {"start": v(5.46, -0.32) * mm, "end": v(5.46, -3.5) * mm});
            skLineSegment(sketch, "E5.0.5.21", {"start": v(-18.92, -0.32) * mm, "end": v(-18.92, -3.5) * mm});
            skLineSegment(sketch, "E5.0.5.22", {"start": v(-40.39, -0.32) * mm, "end": v(-40.39, -3.5) * mm});
            skLineSegment(sketch, "E5.0.5.23", {"start": v(57.15, -0.32) * mm, "end": v(60.32, -0.32) * mm});
            skLineSegment(sketch, "E5.0.5.24", {"start": v(32.77, -0.32) * mm, "end": v(35.94, -0.32) * mm});
            skLineSegment(sketch, "E5.0.5.25", {"start": v(8.38, -0.32) * mm, "end": v(11.56, -0.32) * mm});
            skLineSegment(sketch, "E5.0.5.26", {"start": v(-16, -0.32) * mm, "end": v(-12.83, -0.32) * mm});
            skLineSegment(sketch, "E5.0.5.27", {"start": v(-40.39, -3.5) * mm, "end": v(-37.21, -3.5) * mm});
            skLineSegment(sketch, "E5.0.5.28", {"start": v(57.15, -0.32) * mm, "end": v(57.15, -3.5) * mm});
            skLineSegment(sketch, "E5.0.5.29", {"start": v(32.77, -0.32) * mm, "end": v(32.77, -3.5) * mm});
            skLineSegment(sketch, "E5.0.5.30", {"start": v(8.38, -0.32) * mm, "end": v(8.38, -3.5) * mm});
            skLineSegment(sketch, "E5.0.5.31", {"start": v(-16, -0.32) * mm, "end": v(-16, -3.5) * mm});
            skLineSegment(sketch, "E5.0.5.32", {"start": v(-37.21, -0.32) * mm, "end": v(-37.21, -3.5) * mm});
            skLineSegment(sketch, "E5.0.5.33", {"start": v(57.15, -3.5) * mm, "end": v(60.32, -3.5) * mm});
            skLineSegment(sketch, "E5.0.5.34", {"start": v(32.77, -3.5) * mm, "end": v(35.94, -3.5) * mm});
            skLineSegment(sketch, "E5.0.5.35", {"start": v(8.38, -3.5) * mm, "end": v(11.56, -3.5) * mm});
            skLineSegment(sketch, "E5.0.5.36", {"start": v(-16, -3.5) * mm, "end": v(-12.83, -3.5) * mm});
            skLineSegment(sketch, "E5.0.5.37", {"start": v(-34.29, -0.32) * mm, "end": v(-31.11, -0.32) * mm});
            skLineSegment(sketch, "E5.0.5.38", {"start": v(60.32, -0.32) * mm, "end": v(60.32, -3.5) * mm});
            skLineSegment(sketch, "E5.0.5.39", {"start": v(35.94, -0.32) * mm, "end": v(35.94, -3.5) * mm});
            skLineSegment(sketch, "E5.0.5.40", {"start": v(11.56, -0.32) * mm, "end": v(11.56, -3.5) * mm});
            skLineSegment(sketch, "E5.0.5.41", {"start": v(-12.83, -0.32) * mm, "end": v(-12.83, -3.5) * mm});
            skLineSegment(sketch, "E5.0.5.42", {"start": v(-34.29, -0.32) * mm, "end": v(-34.29, -3.5) * mm});
            skLineSegment(sketch, "E5.0.5.43", {"start": v(38.86, -0.32) * mm, "end": v(42.04, -0.32) * mm});
            skLineSegment(sketch, "E5.0.5.44", {"start": v(14.48, -0.32) * mm, "end": v(17.65, -0.32) * mm});
            skLineSegment(sketch, "E5.0.5.45", {"start": v(-9.9, -0.32) * mm, "end": v(-6.73, -0.32) * mm});
            skLineSegment(sketch, "E5.0.5.46", {"start": v(14.48, -0.32) * mm, "end": v(14.48, -3.5) * mm});
            skLineSegment(sketch, "E5.0.5.47", {"start": v(-9.9, -0.32) * mm, "end": v(-9.9, -3.5) * mm});
            skLineSegment(sketch, "E5.0.5.48", {"start": v(-34.29, -3.5) * mm, "end": v(-31.11, -3.5) * mm});
            skLineSegment(sketch, "E5.0.5.49", {"start": v(38.86, -0.32) * mm, "end": v(38.86, -3.5) * mm});
            skLineSegment(sketch, "E5.0.5.50", {"start": v(14.48, -3.5) * mm, "end": v(17.65, -3.5) * mm});
            skLineSegment(sketch, "E5.0.5.51", {"start": v(-9.9, -3.5) * mm, "end": v(-6.73, -3.5) * mm});
            skLineSegment(sketch, "E5.0.5.52", {"start": v(-31.11, -0.32) * mm, "end": v(-31.11, -3.5) * mm});
            skLineSegment(sketch, "E5.0.5.53", {"start": v(38.86, -3.5) * mm, "end": v(42.04, -3.5) * mm});
            skLineSegment(sketch, "E5.0.5.54", {"start": v(17.65, -0.32) * mm, "end": v(17.65, -3.5) * mm});
            skLineSegment(sketch, "E5.0.5.55", {"start": v(-6.73, -0.32) * mm, "end": v(-6.73, -3.5) * mm});
            skLineSegment(sketch, "E5.0.5.56", {"start": v(-58.67, -0.32) * mm, "end": v(-52.58, -0.32) * mm, "construction": true});
            skLineSegment(sketch, "E5.0.5.57", {"start": v(42.04, -0.32) * mm, "end": v(42.04, -3.5) * mm});
            skLineSegment(sketch, "E5.0.5.58", {"start": v(20.57, -0.32) * mm, "end": v(23.75, -0.32) * mm});
            skLineSegment(sketch, "E5.0.5.59", {"start": v(-3.8, -0.32) * mm, "end": v(-0.63, -0.32) * mm});
            skLineSegment(sketch, "E5.0.5.60", {"start": v(-28.2, -0.32) * mm, "end": v(-25.02, -0.32) * mm});
            skLineSegment(sketch, "E5.0.5.61", {"start": v(44.96, -0.32) * mm, "end": v(48.13, -0.32) * mm});
            skLineSegment(sketch, "E5.0.5.62", {"start": v(20.57, -0.32) * mm, "end": v(20.57, -3.5) * mm});
            skLineSegment(sketch, "E5.0.5.63", {"start": v(-3.8, -0.32) * mm, "end": v(-3.8, -3.5) * mm});
            skLineSegment(sketch, "E5.0.5.64", {"start": v(-28.2, -0.32) * mm, "end": v(-28.2, -3.5) * mm});
            skLineSegment(sketch, "E5.0.5.65", {"start": v(44.96, -0.32) * mm, "end": v(44.96, -3.5) * mm});
            skLineSegment(sketch, "E5.0.5.66", {"start": v(20.57, -3.5) * mm, "end": v(23.75, -3.5) * mm});
            skLineSegment(sketch, "E5.0.5.67", {"start": v(-3.8, -3.5) * mm, "end": v(-0.63, -3.5) * mm});
            skLineSegment(sketch, "E5.0.5.68", {"start": v(-28.2, -3.5) * mm, "end": v(-25.02, -3.5) * mm});
            skLineSegment(sketch, "E5.0.5.69", {"start": v(44.96, -3.5) * mm, "end": v(48.13, -3.5) * mm});
            skLineSegment(sketch, "E5.0.5.70", {"start": v(-46.48, -0.32) * mm, "end": v(-43.3, -0.32) * mm});
            skLineSegment(sketch, "E5.0.5.71", {"start": v(-46.48, -0.32) * mm, "end": v(-46.48, -3.5) * mm});
            skLineSegment(sketch, "E5.0.5.72", {"start": v(-46.48, -3.5) * mm, "end": v(-43.3, -3.5) * mm});
            skLineSegment(sketch, "E5.0.5.73", {"start": v(-58.67, -3.5) * mm, "end": v(-55.5, -3.5) * mm});
            skLineSegment(sketch, "E5.0.5.74", {"start": v(-58.67, -0.32) * mm, "end": v(-58.67, -3.5) * mm});
            skLineSegment(sketch, "E5.0.5.75", {"start": v(-55.5, -0.32) * mm, "end": v(-55.5, -3.5) * mm});
            skLineSegment(sketch, "E5.0.5.76", {"start": v(-52.58, -0.32) * mm, "end": v(-49.4, -0.32) * mm});
            skLineSegment(sketch, "E5.0.5.77", {"start": v(-52.58, -0.32) * mm, "end": v(-52.58, -3.5) * mm});
            skLineSegment(sketch, "E5.0.5.78", {"start": v(-52.58, -3.5) * mm, "end": v(-49.4, -3.5) * mm});
            skLineSegment(sketch, "E5.0.5.79", {"start": v(-49.4, -0.32) * mm, "end": v(-49.4, -3.5) * mm});
            skLineSegment(sketch, "E5.0.5.80", {"start": v(-58.67, -0.32) * mm, "end": v(-55.5, -0.32) * mm});
            skLineSegment(sketch, "E5.0.6.0", {"start": v(48.13, -6.41) * mm, "end": v(48.13, -9.59) * mm});
            skLineSegment(sketch, "E5.0.6.1", {"start": v(23.75, -6.41) * mm, "end": v(23.75, -9.59) * mm});
            skLineSegment(sketch, "E5.0.6.2", {"start": v(-0.63, -6.41) * mm, "end": v(-0.63, -9.59) * mm});
            skLineSegment(sketch, "E5.0.6.3", {"start": v(-25.02, -6.41) * mm, "end": v(-25.02, -9.59) * mm});
            skLineSegment(sketch, "E5.0.6.4", {"start": v(51.05, -6.41) * mm, "end": v(54.23, -6.41) * mm});
            skLineSegment(sketch, "E5.0.6.5", {"start": v(26.67, -6.41) * mm, "end": v(29.84, -6.41) * mm});
            skLineSegment(sketch, "E5.0.6.6", {"start": v(2.29, -6.41) * mm, "end": v(5.46, -6.41) * mm});
            skLineSegment(sketch, "E5.0.6.7", {"start": v(-22.1, -6.41) * mm, "end": v(-18.92, -6.41) * mm});
            skLineSegment(sketch, "E5.0.6.8", {"start": v(51.05, -6.41) * mm, "end": v(51.05, -9.59) * mm});
            skLineSegment(sketch, "E5.0.6.9", {"start": v(26.67, -6.41) * mm, "end": v(26.67, -9.59) * mm});
            skLineSegment(sketch, "E5.0.6.10", {"start": v(2.29, -6.41) * mm, "end": v(2.29, -9.59) * mm});
            skLineSegment(sketch, "E5.0.6.11", {"start": v(-22.1, -6.41) * mm, "end": v(-22.1, -9.59) * mm});
            skLineSegment(sketch, "E5.0.6.12", {"start": v(-43.3, -6.41) * mm, "end": v(-43.3, -9.59) * mm});
            skLineSegment(sketch, "E5.0.6.13", {"start": v(51.05, -9.59) * mm, "end": v(54.23, -9.59) * mm});
            skLineSegment(sketch, "E5.0.6.14", {"start": v(26.67, -9.59) * mm, "end": v(29.84, -9.59) * mm});
            skLineSegment(sketch, "E5.0.6.15", {"start": v(2.29, -9.59) * mm, "end": v(5.46, -9.59) * mm});
            skLineSegment(sketch, "E5.0.6.16", {"start": v(-22.1, -9.59) * mm, "end": v(-18.92, -9.59) * mm});
            skLineSegment(sketch, "E5.0.6.17", {"start": v(-40.39, -6.41) * mm, "end": v(-37.21, -6.41) * mm});
            skLineSegment(sketch, "E5.0.6.18", {"start": v(54.23, -6.41) * mm, "end": v(54.23, -9.59) * mm});
            skLineSegment(sketch, "E5.0.6.19", {"start": v(29.84, -6.41) * mm, "end": v(29.84, -9.59) * mm});
            skLineSegment(sketch, "E5.0.6.20", {"start": v(5.46, -6.41) * mm, "end": v(5.46, -9.59) * mm});
            skLineSegment(sketch, "E5.0.6.21", {"start": v(-18.92, -6.41) * mm, "end": v(-18.92, -9.59) * mm});
            skLineSegment(sketch, "E5.0.6.22", {"start": v(-40.39, -6.41) * mm, "end": v(-40.39, -9.59) * mm});
            skLineSegment(sketch, "E5.0.6.23", {"start": v(57.15, -6.41) * mm, "end": v(60.32, -6.41) * mm});
            skLineSegment(sketch, "E5.0.6.24", {"start": v(32.77, -6.41) * mm, "end": v(35.94, -6.41) * mm});
            skLineSegment(sketch, "E5.0.6.25", {"start": v(8.38, -6.41) * mm, "end": v(11.56, -6.41) * mm});
            skLineSegment(sketch, "E5.0.6.26", {"start": v(-16, -6.41) * mm, "end": v(-12.83, -6.41) * mm});
            skLineSegment(sketch, "E5.0.6.27", {"start": v(-40.39, -9.59) * mm, "end": v(-37.21, -9.59) * mm});
            skLineSegment(sketch, "E5.0.6.28", {"start": v(57.15, -6.41) * mm, "end": v(57.15, -9.59) * mm});
            skLineSegment(sketch, "E5.0.6.29", {"start": v(32.77, -6.41) * mm, "end": v(32.77, -9.59) * mm});
            skLineSegment(sketch, "E5.0.6.30", {"start": v(8.38, -6.41) * mm, "end": v(8.38, -9.59) * mm});
            skLineSegment(sketch, "E5.0.6.31", {"start": v(-16, -6.41) * mm, "end": v(-16, -9.59) * mm});
            skLineSegment(sketch, "E5.0.6.32", {"start": v(-37.21, -6.41) * mm, "end": v(-37.21, -9.59) * mm});
            skLineSegment(sketch, "E5.0.6.33", {"start": v(57.15, -9.59) * mm, "end": v(60.32, -9.59) * mm});
            skLineSegment(sketch, "E5.0.6.34", {"start": v(32.77, -9.59) * mm, "end": v(35.94, -9.59) * mm});
            skLineSegment(sketch, "E5.0.6.35", {"start": v(8.38, -9.59) * mm, "end": v(11.56, -9.59) * mm});
            skLineSegment(sketch, "E5.0.6.36", {"start": v(-16, -9.59) * mm, "end": v(-12.83, -9.59) * mm});
            skLineSegment(sketch, "E5.0.6.37", {"start": v(-34.29, -6.41) * mm, "end": v(-31.11, -6.41) * mm});
            skLineSegment(sketch, "E5.0.6.38", {"start": v(60.32, -6.41) * mm, "end": v(60.32, -9.59) * mm});
            skLineSegment(sketch, "E5.0.6.39", {"start": v(35.94, -6.41) * mm, "end": v(35.94, -9.59) * mm});
            skLineSegment(sketch, "E5.0.6.40", {"start": v(11.56, -6.41) * mm, "end": v(11.56, -9.59) * mm});
            skLineSegment(sketch, "E5.0.6.41", {"start": v(-12.83, -6.41) * mm, "end": v(-12.83, -9.59) * mm});
            skLineSegment(sketch, "E5.0.6.42", {"start": v(-34.29, -6.41) * mm, "end": v(-34.29, -9.59) * mm});
            skLineSegment(sketch, "E5.0.6.43", {"start": v(38.86, -6.41) * mm, "end": v(42.04, -6.41) * mm});
            skLineSegment(sketch, "E5.0.6.44", {"start": v(14.48, -6.41) * mm, "end": v(17.65, -6.41) * mm});
            skLineSegment(sketch, "E5.0.6.45", {"start": v(-9.9, -6.41) * mm, "end": v(-6.73, -6.41) * mm});
            skLineSegment(sketch, "E5.0.6.46", {"start": v(14.48, -6.41) * mm, "end": v(14.48, -9.59) * mm});
            skLineSegment(sketch, "E5.0.6.47", {"start": v(-9.9, -6.41) * mm, "end": v(-9.9, -9.59) * mm});
            skLineSegment(sketch, "E5.0.6.48", {"start": v(-34.29, -9.59) * mm, "end": v(-31.11, -9.59) * mm});
            skLineSegment(sketch, "E5.0.6.49", {"start": v(38.86, -6.41) * mm, "end": v(38.86, -9.59) * mm});
            skLineSegment(sketch, "E5.0.6.50", {"start": v(14.48, -9.59) * mm, "end": v(17.65, -9.59) * mm});
            skLineSegment(sketch, "E5.0.6.51", {"start": v(-9.9, -9.59) * mm, "end": v(-6.73, -9.59) * mm});
            skLineSegment(sketch, "E5.0.6.52", {"start": v(-31.11, -6.41) * mm, "end": v(-31.11, -9.59) * mm});
            skLineSegment(sketch, "E5.0.6.53", {"start": v(38.86, -9.59) * mm, "end": v(42.04, -9.59) * mm});
            skLineSegment(sketch, "E5.0.6.54", {"start": v(17.65, -6.41) * mm, "end": v(17.65, -9.59) * mm});
            skLineSegment(sketch, "E5.0.6.55", {"start": v(-6.73, -6.41) * mm, "end": v(-6.73, -9.59) * mm});
            skLineSegment(sketch, "E5.0.6.56", {"start": v(-58.67, -6.41) * mm, "end": v(-52.58, -6.41) * mm, "construction": true});
            skLineSegment(sketch, "E5.0.6.57", {"start": v(42.04, -6.41) * mm, "end": v(42.04, -9.59) * mm});
            skLineSegment(sketch, "E5.0.6.58", {"start": v(20.57, -6.41) * mm, "end": v(23.75, -6.41) * mm});
            skLineSegment(sketch, "E5.0.6.59", {"start": v(-3.8, -6.41) * mm, "end": v(-0.63, -6.41) * mm});
            skLineSegment(sketch, "E5.0.6.60", {"start": v(-28.2, -6.41) * mm, "end": v(-25.02, -6.41) * mm});
            skLineSegment(sketch, "E5.0.6.61", {"start": v(44.96, -6.41) * mm, "end": v(48.13, -6.41) * mm});
            skLineSegment(sketch, "E5.0.6.62", {"start": v(20.57, -6.41) * mm, "end": v(20.57, -9.59) * mm});
            skLineSegment(sketch, "E5.0.6.63", {"start": v(-3.8, -6.41) * mm, "end": v(-3.8, -9.59) * mm});
            skLineSegment(sketch, "E5.0.6.64", {"start": v(-28.2, -6.41) * mm, "end": v(-28.2, -9.59) * mm});
            skLineSegment(sketch, "E5.0.6.65", {"start": v(44.96, -6.41) * mm, "end": v(44.96, -9.59) * mm});
            skLineSegment(sketch, "E5.0.6.66", {"start": v(20.57, -9.59) * mm, "end": v(23.75, -9.59) * mm});
            skLineSegment(sketch, "E5.0.6.67", {"start": v(-3.8, -9.59) * mm, "end": v(-0.63, -9.59) * mm});
            skLineSegment(sketch, "E5.0.6.68", {"start": v(-28.2, -9.59) * mm, "end": v(-25.02, -9.59) * mm});
            skLineSegment(sketch, "E5.0.6.69", {"start": v(44.96, -9.59) * mm, "end": v(48.13, -9.59) * mm});
            skLineSegment(sketch, "E5.0.6.70", {"start": v(-46.48, -6.41) * mm, "end": v(-43.3, -6.41) * mm});
            skLineSegment(sketch, "E5.0.6.71", {"start": v(-46.48, -6.41) * mm, "end": v(-46.48, -9.59) * mm});
            skLineSegment(sketch, "E5.0.6.72", {"start": v(-46.48, -9.59) * mm, "end": v(-43.3, -9.59) * mm});
            skLineSegment(sketch, "E5.0.6.73", {"start": v(-58.67, -9.59) * mm, "end": v(-55.5, -9.59) * mm});
            skLineSegment(sketch, "E5.0.6.74", {"start": v(-58.67, -6.41) * mm, "end": v(-58.67, -9.59) * mm});
            skLineSegment(sketch, "E5.0.6.75", {"start": v(-55.5, -6.41) * mm, "end": v(-55.5, -9.59) * mm});
            skLineSegment(sketch, "E5.0.6.76", {"start": v(-52.58, -6.41) * mm, "end": v(-49.4, -6.41) * mm});
            skLineSegment(sketch, "E5.0.6.77", {"start": v(-52.58, -6.41) * mm, "end": v(-52.58, -9.59) * mm});
            skLineSegment(sketch, "E5.0.6.78", {"start": v(-52.58, -9.59) * mm, "end": v(-49.4, -9.59) * mm});
            skLineSegment(sketch, "E5.0.6.79", {"start": v(-49.4, -6.41) * mm, "end": v(-49.4, -9.59) * mm});
            skLineSegment(sketch, "E5.0.6.80", {"start": v(-58.67, -6.41) * mm, "end": v(-55.5, -6.41) * mm});
            skLineSegment(sketch, "E5.0.7.0", {"start": v(48.13, -12.5) * mm, "end": v(48.13, -15.68) * mm});
            skLineSegment(sketch, "E5.0.7.1", {"start": v(23.75, -12.5) * mm, "end": v(23.75, -15.68) * mm});
            skLineSegment(sketch, "E5.0.7.2", {"start": v(-0.63, -12.5) * mm, "end": v(-0.63, -15.68) * mm});
            skLineSegment(sketch, "E5.0.7.3", {"start": v(-25.02, -12.5) * mm, "end": v(-25.02, -15.68) * mm});
            skLineSegment(sketch, "E5.0.7.4", {"start": v(51.05, -12.5) * mm, "end": v(54.23, -12.5) * mm});
            skLineSegment(sketch, "E5.0.7.5", {"start": v(26.67, -12.5) * mm, "end": v(29.84, -12.5) * mm});
            skLineSegment(sketch, "E5.0.7.6", {"start": v(2.29, -12.5) * mm, "end": v(5.46, -12.5) * mm});
            skLineSegment(sketch, "E5.0.7.7", {"start": v(-22.1, -12.5) * mm, "end": v(-18.92, -12.5) * mm});
            skLineSegment(sketch, "E5.0.7.8", {"start": v(51.05, -12.5) * mm, "end": v(51.05, -15.68) * mm});
            skLineSegment(sketch, "E5.0.7.9", {"start": v(26.67, -12.5) * mm, "end": v(26.67, -15.68) * mm});
            skLineSegment(sketch, "E5.0.7.10", {"start": v(2.29, -12.5) * mm, "end": v(2.29, -15.68) * mm});
            skLineSegment(sketch, "E5.0.7.11", {"start": v(-22.1, -12.5) * mm, "end": v(-22.1, -15.68) * mm});
            skLineSegment(sketch, "E5.0.7.12", {"start": v(-43.3, -12.5) * mm, "end": v(-43.3, -15.68) * mm});
            skLineSegment(sketch, "E5.0.7.13", {"start": v(51.05, -15.68) * mm, "end": v(54.23, -15.68) * mm});
            skLineSegment(sketch, "E5.0.7.14", {"start": v(26.67, -15.68) * mm, "end": v(29.84, -15.68) * mm});
            skLineSegment(sketch, "E5.0.7.15", {"start": v(2.29, -15.68) * mm, "end": v(5.46, -15.68) * mm});
            skLineSegment(sketch, "E5.0.7.16", {"start": v(-22.1, -15.68) * mm, "end": v(-18.92, -15.68) * mm});
            skLineSegment(sketch, "E5.0.7.17", {"start": v(-40.39, -12.5) * mm, "end": v(-37.21, -12.5) * mm});
            skLineSegment(sketch, "E5.0.7.18", {"start": v(54.23, -12.5) * mm, "end": v(54.23, -15.68) * mm});
            skLineSegment(sketch, "E5.0.7.19", {"start": v(29.84, -12.5) * mm, "end": v(29.84, -15.68) * mm});
            skLineSegment(sketch, "E5.0.7.20", {"start": v(5.46, -12.5) * mm, "end": v(5.46, -15.68) * mm});
            skLineSegment(sketch, "E5.0.7.21", {"start": v(-18.92, -12.5) * mm, "end": v(-18.92, -15.68) * mm});
            skLineSegment(sketch, "E5.0.7.22", {"start": v(-40.39, -12.5) * mm, "end": v(-40.39, -15.68) * mm});
            skLineSegment(sketch, "E5.0.7.23", {"start": v(57.15, -12.5) * mm, "end": v(60.32, -12.5) * mm});
            skLineSegment(sketch, "E5.0.7.24", {"start": v(32.77, -12.5) * mm, "end": v(35.94, -12.5) * mm});
            skLineSegment(sketch, "E5.0.7.25", {"start": v(8.38, -12.5) * mm, "end": v(11.56, -12.5) * mm});
            skLineSegment(sketch, "E5.0.7.26", {"start": v(-16, -12.5) * mm, "end": v(-12.83, -12.5) * mm});
            skLineSegment(sketch, "E5.0.7.27", {"start": v(-40.39, -15.68) * mm, "end": v(-37.21, -15.68) * mm});
            skLineSegment(sketch, "E5.0.7.28", {"start": v(57.15, -12.5) * mm, "end": v(57.15, -15.68) * mm});
            skLineSegment(sketch, "E5.0.7.29", {"start": v(32.77, -12.5) * mm, "end": v(32.77, -15.68) * mm});
            skLineSegment(sketch, "E5.0.7.30", {"start": v(8.38, -12.5) * mm, "end": v(8.38, -15.68) * mm});
            skLineSegment(sketch, "E5.0.7.31", {"start": v(-16, -12.5) * mm, "end": v(-16, -15.68) * mm});
            skLineSegment(sketch, "E5.0.7.32", {"start": v(-37.21, -12.5) * mm, "end": v(-37.21, -15.68) * mm});
            skLineSegment(sketch, "E5.0.7.33", {"start": v(57.15, -15.68) * mm, "end": v(60.32, -15.68) * mm});
            skLineSegment(sketch, "E5.0.7.34", {"start": v(32.77, -15.68) * mm, "end": v(35.94, -15.68) * mm});
            skLineSegment(sketch, "E5.0.7.35", {"start": v(8.38, -15.68) * mm, "end": v(11.56, -15.68) * mm});
            skLineSegment(sketch, "E5.0.7.36", {"start": v(-16, -15.68) * mm, "end": v(-12.83, -15.68) * mm});
            skLineSegment(sketch, "E5.0.7.37", {"start": v(-34.29, -12.5) * mm, "end": v(-31.11, -12.5) * mm});
            skLineSegment(sketch, "E5.0.7.38", {"start": v(60.32, -12.5) * mm, "end": v(60.32, -15.68) * mm});
            skLineSegment(sketch, "E5.0.7.39", {"start": v(35.94, -12.5) * mm, "end": v(35.94, -15.68) * mm});
            skLineSegment(sketch, "E5.0.7.40", {"start": v(11.56, -12.5) * mm, "end": v(11.56, -15.68) * mm});
            skLineSegment(sketch, "E5.0.7.41", {"start": v(-12.83, -12.5) * mm, "end": v(-12.83, -15.68) * mm});
            skLineSegment(sketch, "E5.0.7.42", {"start": v(-34.29, -12.5) * mm, "end": v(-34.29, -15.68) * mm});
            skLineSegment(sketch, "E5.0.7.43", {"start": v(38.86, -12.5) * mm, "end": v(42.04, -12.5) * mm});
            skLineSegment(sketch, "E5.0.7.44", {"start": v(14.48, -12.5) * mm, "end": v(17.65, -12.5) * mm});
            skLineSegment(sketch, "E5.0.7.45", {"start": v(-9.9, -12.5) * mm, "end": v(-6.73, -12.5) * mm});
            skLineSegment(sketch, "E5.0.7.46", {"start": v(14.48, -12.5) * mm, "end": v(14.48, -15.68) * mm});
            skLineSegment(sketch, "E5.0.7.47", {"start": v(-9.9, -12.5) * mm, "end": v(-9.9, -15.68) * mm});
            skLineSegment(sketch, "E5.0.7.48", {"start": v(-34.29, -15.68) * mm, "end": v(-31.11, -15.68) * mm});
            skLineSegment(sketch, "E5.0.7.49", {"start": v(38.86, -12.5) * mm, "end": v(38.86, -15.68) * mm});
            skLineSegment(sketch, "E5.0.7.50", {"start": v(14.48, -15.68) * mm, "end": v(17.65, -15.68) * mm});
            skLineSegment(sketch, "E5.0.7.51", {"start": v(-9.9, -15.68) * mm, "end": v(-6.73, -15.68) * mm});
            skLineSegment(sketch, "E5.0.7.52", {"start": v(-31.11, -12.5) * mm, "end": v(-31.11, -15.68) * mm});
            skLineSegment(sketch, "E5.0.7.53", {"start": v(38.86, -15.68) * mm, "end": v(42.04, -15.68) * mm});
            skLineSegment(sketch, "E5.0.7.54", {"start": v(17.65, -12.5) * mm, "end": v(17.65, -15.68) * mm});
            skLineSegment(sketch, "E5.0.7.55", {"start": v(-6.73, -12.5) * mm, "end": v(-6.73, -15.68) * mm});
            skLineSegment(sketch, "E5.0.7.56", {"start": v(-58.67, -12.5) * mm, "end": v(-52.58, -12.5) * mm, "construction": true});
            skLineSegment(sketch, "E5.0.7.57", {"start": v(42.04, -12.5) * mm, "end": v(42.04, -15.68) * mm});
            skLineSegment(sketch, "E5.0.7.58", {"start": v(20.57, -12.5) * mm, "end": v(23.75, -12.5) * mm});
            skLineSegment(sketch, "E5.0.7.59", {"start": v(-3.8, -12.5) * mm, "end": v(-0.63, -12.5) * mm});
            skLineSegment(sketch, "E5.0.7.60", {"start": v(-28.2, -12.5) * mm, "end": v(-25.02, -12.5) * mm});
            skLineSegment(sketch, "E5.0.7.61", {"start": v(44.96, -12.5) * mm, "end": v(48.13, -12.5) * mm});
            skLineSegment(sketch, "E5.0.7.62", {"start": v(20.57, -12.5) * mm, "end": v(20.57, -15.68) * mm});
            skLineSegment(sketch, "E5.0.7.63", {"start": v(-3.8, -12.5) * mm, "end": v(-3.8, -15.68) * mm});
            skLineSegment(sketch, "E5.0.7.64", {"start": v(-28.2, -12.5) * mm, "end": v(-28.2, -15.68) * mm});
            skLineSegment(sketch, "E5.0.7.65", {"start": v(44.96, -12.5) * mm, "end": v(44.96, -15.68) * mm});
            skLineSegment(sketch, "E5.0.7.66", {"start": v(20.57, -15.68) * mm, "end": v(23.75, -15.68) * mm});
            skLineSegment(sketch, "E5.0.7.67", {"start": v(-3.8, -15.68) * mm, "end": v(-0.63, -15.68) * mm});
            skLineSegment(sketch, "E5.0.7.68", {"start": v(-28.2, -15.68) * mm, "end": v(-25.02, -15.68) * mm});
            skLineSegment(sketch, "E5.0.7.69", {"start": v(44.96, -15.68) * mm, "end": v(48.13, -15.68) * mm});
            skLineSegment(sketch, "E5.0.7.70", {"start": v(-46.48, -12.5) * mm, "end": v(-43.3, -12.5) * mm});
            skLineSegment(sketch, "E5.0.7.71", {"start": v(-46.48, -12.5) * mm, "end": v(-46.48, -15.68) * mm});
            skLineSegment(sketch, "E5.0.7.72", {"start": v(-46.48, -15.68) * mm, "end": v(-43.3, -15.68) * mm});
            skLineSegment(sketch, "E5.0.7.73", {"start": v(-58.67, -15.68) * mm, "end": v(-55.5, -15.68) * mm});
            skLineSegment(sketch, "E5.0.7.74", {"start": v(-58.67, -12.5) * mm, "end": v(-58.67, -15.68) * mm});
            skLineSegment(sketch, "E5.0.7.75", {"start": v(-55.5, -12.5) * mm, "end": v(-55.5, -15.68) * mm});
            skLineSegment(sketch, "E5.0.7.76", {"start": v(-52.58, -12.5) * mm, "end": v(-49.4, -12.5) * mm});
            skLineSegment(sketch, "E5.0.7.77", {"start": v(-52.58, -12.5) * mm, "end": v(-52.58, -15.68) * mm});
            skLineSegment(sketch, "E5.0.7.78", {"start": v(-52.58, -15.68) * mm, "end": v(-49.4, -15.68) * mm});
            skLineSegment(sketch, "E5.0.7.79", {"start": v(-49.4, -12.5) * mm, "end": v(-49.4, -15.68) * mm});
            skLineSegment(sketch, "E5.0.7.80", {"start": v(-58.67, -12.5) * mm, "end": v(-55.5, -12.5) * mm});
            skLineSegment(sketch, "E5.0.8.0", {"start": v(48.13, -18.6) * mm, "end": v(48.13, -21.78) * mm});
            skLineSegment(sketch, "E5.0.8.1", {"start": v(23.75, -18.6) * mm, "end": v(23.75, -21.78) * mm});
            skLineSegment(sketch, "E5.0.8.2", {"start": v(-0.63, -18.6) * mm, "end": v(-0.63, -21.78) * mm});
            skLineSegment(sketch, "E5.0.8.3", {"start": v(-25.02, -18.6) * mm, "end": v(-25.02, -21.78) * mm});
            skLineSegment(sketch, "E5.0.8.4", {"start": v(51.05, -18.6) * mm, "end": v(54.23, -18.6) * mm});
            skLineSegment(sketch, "E5.0.8.5", {"start": v(26.67, -18.6) * mm, "end": v(29.84, -18.6) * mm});
            skLineSegment(sketch, "E5.0.8.6", {"start": v(2.29, -18.6) * mm, "end": v(5.46, -18.6) * mm});
            skLineSegment(sketch, "E5.0.8.7", {"start": v(-22.1, -18.6) * mm, "end": v(-18.92, -18.6) * mm});
            skLineSegment(sketch, "E5.0.8.8", {"start": v(51.05, -18.6) * mm, "end": v(51.05, -21.78) * mm});
            skLineSegment(sketch, "E5.0.8.9", {"start": v(26.67, -18.6) * mm, "end": v(26.67, -21.78) * mm});
            skLineSegment(sketch, "E5.0.8.10", {"start": v(2.29, -18.6) * mm, "end": v(2.29, -21.78) * mm});
            skLineSegment(sketch, "E5.0.8.11", {"start": v(-22.1, -18.6) * mm, "end": v(-22.1, -21.78) * mm});
            skLineSegment(sketch, "E5.0.8.12", {"start": v(-43.3, -18.6) * mm, "end": v(-43.3, -21.78) * mm});
            skLineSegment(sketch, "E5.0.8.13", {"start": v(51.05, -21.78) * mm, "end": v(54.23, -21.78) * mm});
            skLineSegment(sketch, "E5.0.8.14", {"start": v(26.67, -21.78) * mm, "end": v(29.84, -21.78) * mm});
            skLineSegment(sketch, "E5.0.8.15", {"start": v(2.29, -21.78) * mm, "end": v(5.46, -21.78) * mm});
            skLineSegment(sketch, "E5.0.8.16", {"start": v(-22.1, -21.78) * mm, "end": v(-18.92, -21.78) * mm});
            skLineSegment(sketch, "E5.0.8.17", {"start": v(-40.39, -18.6) * mm, "end": v(-37.21, -18.6) * mm});
            skLineSegment(sketch, "E5.0.8.18", {"start": v(54.23, -18.6) * mm, "end": v(54.23, -21.78) * mm});
            skLineSegment(sketch, "E5.0.8.19", {"start": v(29.84, -18.6) * mm, "end": v(29.84, -21.78) * mm});
            skLineSegment(sketch, "E5.0.8.20", {"start": v(5.46, -18.6) * mm, "end": v(5.46, -21.78) * mm});
            skLineSegment(sketch, "E5.0.8.21", {"start": v(-18.92, -18.6) * mm, "end": v(-18.92, -21.78) * mm});
            skLineSegment(sketch, "E5.0.8.22", {"start": v(-40.39, -18.6) * mm, "end": v(-40.39, -21.78) * mm});
            skLineSegment(sketch, "E5.0.8.23", {"start": v(57.15, -18.6) * mm, "end": v(60.32, -18.6) * mm});
            skLineSegment(sketch, "E5.0.8.24", {"start": v(32.77, -18.6) * mm, "end": v(35.94, -18.6) * mm});
            skLineSegment(sketch, "E5.0.8.25", {"start": v(8.38, -18.6) * mm, "end": v(11.56, -18.6) * mm});
            skLineSegment(sketch, "E5.0.8.26", {"start": v(-16, -18.6) * mm, "end": v(-12.83, -18.6) * mm});
            skLineSegment(sketch, "E5.0.8.27", {"start": v(-40.39, -21.78) * mm, "end": v(-37.21, -21.78) * mm});
            skLineSegment(sketch, "E5.0.8.28", {"start": v(57.15, -18.6) * mm, "end": v(57.15, -21.78) * mm});
            skLineSegment(sketch, "E5.0.8.29", {"start": v(32.77, -18.6) * mm, "end": v(32.77, -21.78) * mm});
            skLineSegment(sketch, "E5.0.8.30", {"start": v(8.38, -18.6) * mm, "end": v(8.38, -21.78) * mm});
            skLineSegment(sketch, "E5.0.8.31", {"start": v(-16, -18.6) * mm, "end": v(-16, -21.78) * mm});
            skLineSegment(sketch, "E5.0.8.32", {"start": v(-37.21, -18.6) * mm, "end": v(-37.21, -21.78) * mm});
            skLineSegment(sketch, "E5.0.8.33", {"start": v(57.15, -21.78) * mm, "end": v(60.32, -21.78) * mm});
            skLineSegment(sketch, "E5.0.8.34", {"start": v(32.77, -21.78) * mm, "end": v(35.94, -21.78) * mm});
            skLineSegment(sketch, "E5.0.8.35", {"start": v(8.38, -21.78) * mm, "end": v(11.56, -21.78) * mm});
            skLineSegment(sketch, "E5.0.8.36", {"start": v(-16, -21.78) * mm, "end": v(-12.83, -21.78) * mm});
            skLineSegment(sketch, "E5.0.8.37", {"start": v(-34.29, -18.6) * mm, "end": v(-31.11, -18.6) * mm});
            skLineSegment(sketch, "E5.0.8.38", {"start": v(60.32, -18.6) * mm, "end": v(60.32, -21.78) * mm});
            skLineSegment(sketch, "E5.0.8.39", {"start": v(35.94, -18.6) * mm, "end": v(35.94, -21.78) * mm});
            skLineSegment(sketch, "E5.0.8.40", {"start": v(11.56, -18.6) * mm, "end": v(11.56, -21.78) * mm});
            skLineSegment(sketch, "E5.0.8.41", {"start": v(-12.83, -18.6) * mm, "end": v(-12.83, -21.78) * mm});
            skLineSegment(sketch, "E5.0.8.42", {"start": v(-34.29, -18.6) * mm, "end": v(-34.29, -21.78) * mm});
            skLineSegment(sketch, "E5.0.8.43", {"start": v(38.86, -18.6) * mm, "end": v(42.04, -18.6) * mm});
            skLineSegment(sketch, "E5.0.8.44", {"start": v(14.48, -18.6) * mm, "end": v(17.65, -18.6) * mm});
            skLineSegment(sketch, "E5.0.8.45", {"start": v(-9.9, -18.6) * mm, "end": v(-6.73, -18.6) * mm});
            skLineSegment(sketch, "E5.0.8.46", {"start": v(14.48, -18.6) * mm, "end": v(14.48, -21.78) * mm});
            skLineSegment(sketch, "E5.0.8.47", {"start": v(-9.9, -18.6) * mm, "end": v(-9.9, -21.78) * mm});
            skLineSegment(sketch, "E5.0.8.48", {"start": v(-34.29, -21.78) * mm, "end": v(-31.11, -21.78) * mm});
            skLineSegment(sketch, "E5.0.8.49", {"start": v(38.86, -18.6) * mm, "end": v(38.86, -21.78) * mm});
            skLineSegment(sketch, "E5.0.8.50", {"start": v(14.48, -21.78) * mm, "end": v(17.65, -21.78) * mm});
            skLineSegment(sketch, "E5.0.8.51", {"start": v(-9.9, -21.78) * mm, "end": v(-6.73, -21.78) * mm});
            skLineSegment(sketch, "E5.0.8.52", {"start": v(-31.11, -18.6) * mm, "end": v(-31.11, -21.78) * mm});
            skLineSegment(sketch, "E5.0.8.53", {"start": v(38.86, -21.78) * mm, "end": v(42.04, -21.78) * mm});
            skLineSegment(sketch, "E5.0.8.54", {"start": v(17.65, -18.6) * mm, "end": v(17.65, -21.78) * mm});
            skLineSegment(sketch, "E5.0.8.55", {"start": v(-6.73, -18.6) * mm, "end": v(-6.73, -21.78) * mm});
            skLineSegment(sketch, "E5.0.8.56", {"start": v(-58.67, -18.6) * mm, "end": v(-52.58, -18.6) * mm, "construction": true});
            skLineSegment(sketch, "E5.0.8.57", {"start": v(42.04, -18.6) * mm, "end": v(42.04, -21.78) * mm});
            skLineSegment(sketch, "E5.0.8.58", {"start": v(20.57, -18.6) * mm, "end": v(23.75, -18.6) * mm});
            skLineSegment(sketch, "E5.0.8.59", {"start": v(-3.8, -18.6) * mm, "end": v(-0.63, -18.6) * mm});
            skLineSegment(sketch, "E5.0.8.60", {"start": v(-28.2, -18.6) * mm, "end": v(-25.02, -18.6) * mm});
            skLineSegment(sketch, "E5.0.8.61", {"start": v(44.96, -18.6) * mm, "end": v(48.13, -18.6) * mm});
            skLineSegment(sketch, "E5.0.8.62", {"start": v(20.57, -18.6) * mm, "end": v(20.57, -21.78) * mm});
            skLineSegment(sketch, "E5.0.8.63", {"start": v(-3.8, -18.6) * mm, "end": v(-3.8, -21.78) * mm});
            skLineSegment(sketch, "E5.0.8.64", {"start": v(-28.2, -18.6) * mm, "end": v(-28.2, -21.78) * mm});
            skLineSegment(sketch, "E5.0.8.65", {"start": v(44.96, -18.6) * mm, "end": v(44.96, -21.78) * mm});
            skLineSegment(sketch, "E5.0.8.66", {"start": v(20.57, -21.78) * mm, "end": v(23.75, -21.78) * mm});
            skLineSegment(sketch, "E5.0.8.67", {"start": v(-3.8, -21.78) * mm, "end": v(-0.63, -21.78) * mm});
            skLineSegment(sketch, "E5.0.8.68", {"start": v(-28.2, -21.78) * mm, "end": v(-25.02, -21.78) * mm});
            skLineSegment(sketch, "E5.0.8.69", {"start": v(44.96, -21.78) * mm, "end": v(48.13, -21.78) * mm});
            skLineSegment(sketch, "E5.0.8.70", {"start": v(-46.48, -18.6) * mm, "end": v(-43.3, -18.6) * mm});
            skLineSegment(sketch, "E5.0.8.71", {"start": v(-46.48, -18.6) * mm, "end": v(-46.48, -21.78) * mm});
            skLineSegment(sketch, "E5.0.8.72", {"start": v(-46.48, -21.78) * mm, "end": v(-43.3, -21.78) * mm});
            skLineSegment(sketch, "E5.0.8.73", {"start": v(-58.67, -21.78) * mm, "end": v(-55.5, -21.78) * mm});
            skLineSegment(sketch, "E5.0.8.74", {"start": v(-58.67, -18.6) * mm, "end": v(-58.67, -21.78) * mm});
            skLineSegment(sketch, "E5.0.8.75", {"start": v(-55.5, -18.6) * mm, "end": v(-55.5, -21.78) * mm});
            skLineSegment(sketch, "E5.0.8.76", {"start": v(-52.58, -18.6) * mm, "end": v(-49.4, -18.6) * mm});
            skLineSegment(sketch, "E5.0.8.77", {"start": v(-52.58, -18.6) * mm, "end": v(-52.58, -21.78) * mm});
            skLineSegment(sketch, "E5.0.8.78", {"start": v(-52.58, -21.78) * mm, "end": v(-49.4, -21.78) * mm});
            skLineSegment(sketch, "E5.0.8.79", {"start": v(-49.4, -18.6) * mm, "end": v(-49.4, -21.78) * mm});
            skLineSegment(sketch, "E5.0.8.80", {"start": v(-58.67, -18.6) * mm, "end": v(-55.5, -18.6) * mm});
            skLineSegment(sketch, "E5.0.9.0", {"start": v(48.13, -24.7) * mm, "end": v(48.13, -27.88) * mm});
            skLineSegment(sketch, "E5.0.9.1", {"start": v(23.75, -24.7) * mm, "end": v(23.75, -27.88) * mm});
            skLineSegment(sketch, "E5.0.9.2", {"start": v(-0.63, -24.7) * mm, "end": v(-0.63, -27.88) * mm});
            skLineSegment(sketch, "E5.0.9.3", {"start": v(-25.02, -24.7) * mm, "end": v(-25.02, -27.88) * mm});
            skLineSegment(sketch, "E5.0.9.4", {"start": v(51.05, -24.7) * mm, "end": v(54.23, -24.7) * mm});
            skLineSegment(sketch, "E5.0.9.5", {"start": v(26.67, -24.7) * mm, "end": v(29.84, -24.7) * mm});
            skLineSegment(sketch, "E5.0.9.6", {"start": v(2.29, -24.7) * mm, "end": v(5.46, -24.7) * mm});
            skLineSegment(sketch, "E5.0.9.7", {"start": v(-22.1, -24.7) * mm, "end": v(-18.92, -24.7) * mm});
            skLineSegment(sketch, "E5.0.9.8", {"start": v(51.05, -24.7) * mm, "end": v(51.05, -27.88) * mm});
            skLineSegment(sketch, "E5.0.9.9", {"start": v(26.67, -24.7) * mm, "end": v(26.67, -27.88) * mm});
            skLineSegment(sketch, "E5.0.9.10", {"start": v(2.29, -24.7) * mm, "end": v(2.29, -27.88) * mm});
            skLineSegment(sketch, "E5.0.9.11", {"start": v(-22.1, -24.7) * mm, "end": v(-22.1, -27.88) * mm});
            skLineSegment(sketch, "E5.0.9.12", {"start": v(-43.3, -24.7) * mm, "end": v(-43.3, -27.88) * mm});
            skLineSegment(sketch, "E5.0.9.13", {"start": v(51.05, -27.88) * mm, "end": v(54.23, -27.88) * mm});
            skLineSegment(sketch, "E5.0.9.14", {"start": v(26.67, -27.88) * mm, "end": v(29.84, -27.88) * mm});
            skLineSegment(sketch, "E5.0.9.15", {"start": v(2.29, -27.88) * mm, "end": v(5.46, -27.88) * mm});
            skLineSegment(sketch, "E5.0.9.16", {"start": v(-22.1, -27.88) * mm, "end": v(-18.92, -27.88) * mm});
            skLineSegment(sketch, "E5.0.9.17", {"start": v(-40.39, -24.7) * mm, "end": v(-37.21, -24.7) * mm});
            skLineSegment(sketch, "E5.0.9.18", {"start": v(54.23, -24.7) * mm, "end": v(54.23, -27.88) * mm});
            skLineSegment(sketch, "E5.0.9.19", {"start": v(29.84, -24.7) * mm, "end": v(29.84, -27.88) * mm});
            skLineSegment(sketch, "E5.0.9.20", {"start": v(5.46, -24.7) * mm, "end": v(5.46, -27.88) * mm});
            skLineSegment(sketch, "E5.0.9.21", {"start": v(-18.92, -24.7) * mm, "end": v(-18.92, -27.88) * mm});
            skLineSegment(sketch, "E5.0.9.22", {"start": v(-40.39, -24.7) * mm, "end": v(-40.39, -27.88) * mm});
            skLineSegment(sketch, "E5.0.9.23", {"start": v(57.15, -24.7) * mm, "end": v(60.32, -24.7) * mm});
            skLineSegment(sketch, "E5.0.9.24", {"start": v(32.77, -24.7) * mm, "end": v(35.94, -24.7) * mm});
            skLineSegment(sketch, "E5.0.9.25", {"start": v(8.38, -24.7) * mm, "end": v(11.56, -24.7) * mm});
            skLineSegment(sketch, "E5.0.9.26", {"start": v(-16, -24.7) * mm, "end": v(-12.83, -24.7) * mm});
            skLineSegment(sketch, "E5.0.9.27", {"start": v(-40.39, -27.88) * mm, "end": v(-37.21, -27.88) * mm});
            skLineSegment(sketch, "E5.0.9.28", {"start": v(57.15, -24.7) * mm, "end": v(57.15, -27.88) * mm});
            skLineSegment(sketch, "E5.0.9.29", {"start": v(32.77, -24.7) * mm, "end": v(32.77, -27.88) * mm});
            skLineSegment(sketch, "E5.0.9.30", {"start": v(8.38, -24.7) * mm, "end": v(8.38, -27.88) * mm});
            skLineSegment(sketch, "E5.0.9.31", {"start": v(-16, -24.7) * mm, "end": v(-16, -27.88) * mm});
            skLineSegment(sketch, "E5.0.9.32", {"start": v(-37.21, -24.7) * mm, "end": v(-37.21, -27.88) * mm});
            skLineSegment(sketch, "E5.0.9.33", {"start": v(57.15, -27.88) * mm, "end": v(60.32, -27.88) * mm});
            skLineSegment(sketch, "E5.0.9.34", {"start": v(32.77, -27.88) * mm, "end": v(35.94, -27.88) * mm});
            skLineSegment(sketch, "E5.0.9.35", {"start": v(8.38, -27.88) * mm, "end": v(11.56, -27.88) * mm});
            skLineSegment(sketch, "E5.0.9.36", {"start": v(-16, -27.88) * mm, "end": v(-12.83, -27.88) * mm});
            skLineSegment(sketch, "E5.0.9.37", {"start": v(-34.29, -24.7) * mm, "end": v(-31.11, -24.7) * mm});
            skLineSegment(sketch, "E5.0.9.38", {"start": v(60.32, -24.7) * mm, "end": v(60.32, -27.88) * mm});
            skLineSegment(sketch, "E5.0.9.39", {"start": v(35.94, -24.7) * mm, "end": v(35.94, -27.88) * mm});
            skLineSegment(sketch, "E5.0.9.40", {"start": v(11.56, -24.7) * mm, "end": v(11.56, -27.88) * mm});
            skLineSegment(sketch, "E5.0.9.41", {"start": v(-12.83, -24.7) * mm, "end": v(-12.83, -27.88) * mm});
            skLineSegment(sketch, "E5.0.9.42", {"start": v(-34.29, -24.7) * mm, "end": v(-34.29, -27.88) * mm});
            skLineSegment(sketch, "E5.0.9.43", {"start": v(38.86, -24.7) * mm, "end": v(42.04, -24.7) * mm});
            skLineSegment(sketch, "E5.0.9.44", {"start": v(14.48, -24.7) * mm, "end": v(17.65, -24.7) * mm});
            skLineSegment(sketch, "E5.0.9.45", {"start": v(-9.9, -24.7) * mm, "end": v(-6.73, -24.7) * mm});
            skLineSegment(sketch, "E5.0.9.46", {"start": v(14.48, -24.7) * mm, "end": v(14.48, -27.88) * mm});
            skLineSegment(sketch, "E5.0.9.47", {"start": v(-9.9, -24.7) * mm, "end": v(-9.9, -27.88) * mm});
            skLineSegment(sketch, "E5.0.9.48", {"start": v(-34.29, -27.88) * mm, "end": v(-31.11, -27.88) * mm});
            skLineSegment(sketch, "E5.0.9.49", {"start": v(38.86, -24.7) * mm, "end": v(38.86, -27.88) * mm});
            skLineSegment(sketch, "E5.0.9.50", {"start": v(14.48, -27.88) * mm, "end": v(17.65, -27.88) * mm});
            skLineSegment(sketch, "E5.0.9.51", {"start": v(-9.9, -27.88) * mm, "end": v(-6.73, -27.88) * mm});
            skLineSegment(sketch, "E5.0.9.52", {"start": v(-31.11, -24.7) * mm, "end": v(-31.11, -27.88) * mm});
            skLineSegment(sketch, "E5.0.9.53", {"start": v(38.86, -27.88) * mm, "end": v(42.04, -27.88) * mm});
            skLineSegment(sketch, "E5.0.9.54", {"start": v(17.65, -24.7) * mm, "end": v(17.65, -27.88) * mm});
            skLineSegment(sketch, "E5.0.9.55", {"start": v(-6.73, -24.7) * mm, "end": v(-6.73, -27.88) * mm});
            skLineSegment(sketch, "E5.0.9.56", {"start": v(-58.67, -24.7) * mm, "end": v(-52.58, -24.7) * mm, "construction": true});
            skLineSegment(sketch, "E5.0.9.57", {"start": v(42.04, -24.7) * mm, "end": v(42.04, -27.88) * mm});
            skLineSegment(sketch, "E5.0.9.58", {"start": v(20.57, -24.7) * mm, "end": v(23.75, -24.7) * mm});
            skLineSegment(sketch, "E5.0.9.59", {"start": v(-3.8, -24.7) * mm, "end": v(-0.63, -24.7) * mm});
            skLineSegment(sketch, "E5.0.9.60", {"start": v(-28.2, -24.7) * mm, "end": v(-25.02, -24.7) * mm});
            skLineSegment(sketch, "E5.0.9.61", {"start": v(44.96, -24.7) * mm, "end": v(48.13, -24.7) * mm});
            skLineSegment(sketch, "E5.0.9.62", {"start": v(20.57, -24.7) * mm, "end": v(20.57, -27.88) * mm});
            skLineSegment(sketch, "E5.0.9.63", {"start": v(-3.8, -24.7) * mm, "end": v(-3.8, -27.88) * mm});
            skLineSegment(sketch, "E5.0.9.64", {"start": v(-28.2, -24.7) * mm, "end": v(-28.2, -27.88) * mm});
            skLineSegment(sketch, "E5.0.9.65", {"start": v(44.96, -24.7) * mm, "end": v(44.96, -27.88) * mm});
            skLineSegment(sketch, "E5.0.9.66", {"start": v(20.57, -27.88) * mm, "end": v(23.75, -27.88) * mm});
            skLineSegment(sketch, "E5.0.9.67", {"start": v(-3.8, -27.88) * mm, "end": v(-0.63, -27.88) * mm});
            skLineSegment(sketch, "E5.0.9.68", {"start": v(-28.2, -27.88) * mm, "end": v(-25.02, -27.88) * mm});
            skLineSegment(sketch, "E5.0.9.69", {"start": v(44.96, -27.88) * mm, "end": v(48.13, -27.88) * mm});
            skLineSegment(sketch, "E5.0.9.70", {"start": v(-46.48, -24.7) * mm, "end": v(-43.3, -24.7) * mm});
            skLineSegment(sketch, "E5.0.9.71", {"start": v(-46.48, -24.7) * mm, "end": v(-46.48, -27.88) * mm});
            skLineSegment(sketch, "E5.0.9.72", {"start": v(-46.48, -27.88) * mm, "end": v(-43.3, -27.88) * mm});
            skLineSegment(sketch, "E5.0.9.73", {"start": v(-58.67, -27.88) * mm, "end": v(-55.5, -27.88) * mm});
            skLineSegment(sketch, "E5.0.9.74", {"start": v(-58.67, -24.7) * mm, "end": v(-58.67, -27.88) * mm});
            skLineSegment(sketch, "E5.0.9.75", {"start": v(-55.5, -24.7) * mm, "end": v(-55.5, -27.88) * mm});
            skLineSegment(sketch, "E5.0.9.76", {"start": v(-52.58, -24.7) * mm, "end": v(-49.4, -24.7) * mm});
            skLineSegment(sketch, "E5.0.9.77", {"start": v(-52.58, -24.7) * mm, "end": v(-52.58, -27.88) * mm});
            skLineSegment(sketch, "E5.0.9.78", {"start": v(-52.58, -27.88) * mm, "end": v(-49.4, -27.88) * mm});
            skLineSegment(sketch, "E5.0.9.79", {"start": v(-49.4, -24.7) * mm, "end": v(-49.4, -27.88) * mm});
            skLineSegment(sketch, "E5.0.9.80", {"start": v(-58.67, -24.7) * mm, "end": v(-55.5, -24.7) * mm});
            skLineSegment(sketch, "E5.direction1", {"start": v(-58.67, 26.99) * mm, "end": v(-33.27, 26.99) * mm, "construction": true});
            skLineSegment(sketch, "E5.direction2", {"start": v(-58.67, 26.99) * mm, "end": v(-58.67, 20.9) * mm, "construction": true});
            skSolve(sketch);
        }
        {
            var Q0;
            Q0=makeQuery(id+"F0.imprint","IMPRINT",FACE,{"disambiguationData":[TD([[makeQuery(id+"F0.imprint","IMPRINT",EDGE,{"derivedFrom":sQuery(id+"F0.wireOp",EDGE,"E0.bottom")}),-1.0]])]});
            extrude(context, id + "F1", {"entities" : qUnion([Q0]), "depth" : 3.17 * mm});
        }
        {
            var Q0;
            Q0=makeQuery(id+"F1.opExtrude","CAP_FACE",FACE,{"disambiguationData":[OSD([sQuery(id+"F0.wireOp",EDGE,"E0.bottom"),sQuery(id+"F0.wireOp",EDGE,"E0.top"),sQuery(id+"F0.wireOp",EDGE,"E0.left"),sQuery(id+"F0.wireOp",EDGE,"E0.right"),sQuery(id+"F0.wireOp",EDGE,"E1.bottom"),sQuery(id+"F0.wireOp",EDGE,"E1.top"),sQuery(id+"F0.wireOp",EDGE,"E1.left"),sQuery(id+"F0.wireOp",EDGE,"E1.right"),sQuery(id+"F0.wireOp",EDGE,"E2.1.0.0"),sQuery(id+"F0.wireOp",EDGE,"E2.1.0.1"),sQuery(id+"F0.wireOp",EDGE,"E2.1.0.2"),sQuery(id+"F0.wireOp",EDGE,"E2.1.0.3"),sQuery(id+"F0.wireOp",EDGE,"E2.2.0.0"),sQuery(id+"F0.wireOp",EDGE,"E2.2.0.1"),sQuery(id+"F0.wireOp",EDGE,"E2.2.0.2"),sQuery(id+"F0.wireOp",EDGE,"E2.2.0.3"),sQuery(id+"F0.wireOp",EDGE,"E2.3.0.0"),sQuery(id+"F0.wireOp",EDGE,"E2.3.0.1"),sQuery(id+"F0.wireOp",EDGE,"E2.3.0.2"),sQuery(id+"F0.wireOp",EDGE,"E2.3.0.3"),sQuery(id+"F0.wireOp",EDGE,"E2.4.0.0"),sQuery(id+"F0.wireOp",EDGE,"E2.4.0.1"),sQuery(id+"F0.wireOp",EDGE,"E2.4.0.2"),sQuery(id+"F0.wireOp",EDGE,"E2.4.0.3"),sQuery(id+"F0.wireOp",EDGE,"E3.0.5.0"),sQuery(id+"F0.wireOp",EDGE,"E3.3.5.0"),sQuery(id+"F0.wireOp",EDGE,"E3.6.5.0"),sQuery(id+"F0.wireOp",EDGE,"E3.9.5.0"),sQuery(id+"F0.wireOp",EDGE,"E3.0.6.0"),sQuery(id+"F0.wireOp",EDGE,"E3.3.6.0"),sQuery(id+"F0.wireOp",EDGE,"E3.6.6.0"),sQuery(id+"F0.wireOp",EDGE,"E3.9.6.0"),sQuery(id+"F0.wireOp",EDGE,"E3.0.7.0"),sQuery(id+"F0.wireOp",EDGE,"E3.3.7.0"),sQuery(id+"F0.wireOp",EDGE,"E3.6.7.0"),sQuery(id+"F0.wireOp",EDGE,"E3.9.7.0"),sQuery(id+"F0.wireOp",EDGE,"E3.0.8.0"),sQuery(id+"F0.wireOp",EDGE,"E3.3.8.0"),sQuery(id+"F0.wireOp",EDGE,"E3.6.8.0"),sQuery(id+"F0.wireOp",EDGE,"E3.9.8.0"),sQuery(id+"F0.wireOp",EDGE,"E3.0.9.0"),sQuery(id+"F0.wireOp",EDGE,"E3.3.9.0"),sQuery(id+"F0.wireOp",EDGE,"E3.6.9.0"),sQuery(id+"F0.wireOp",EDGE,"E3.9.9.0"),sQuery(id+"F0.wireOp",EDGE,"E4.0.10.0"),sQuery(id+"F0.wireOp",EDGE,"E4.3.10.0"),sQuery(id+"F0.wireOp",EDGE,"E4.6.10.0"),sQuery(id+"F0.wireOp",EDGE,"E4.9.10.0"),sQuery(id+"F0.wireOp",EDGE,"E4.0.11.0"),sQuery(id+"F0.wireOp",EDGE,"E4.3.11.0"),sQuery(id+"F0.wireOp",EDGE,"E4.6.11.0"),sQuery(id+"F0.wireOp",EDGE,"E4.9.11.0"),sQuery(id+"F0.wireOp",EDGE,"E4.0.12.0"),sQuery(id+"F0.wireOp",EDGE,"E4.3.12.0"),sQuery(id+"F0.wireOp",EDGE,"E4.6.12.0"),sQuery(id+"F0.wireOp",EDGE,"E4.9.12.0"),sQuery(id+"F0.wireOp",EDGE,"E4.0.13.0"),sQuery(id+"F0.wireOp",EDGE,"E4.3.13.0"),sQuery(id+"F0.wireOp",EDGE,"E4.6.13.0"),sQuery(id+"F0.wireOp",EDGE,"E4.9.13.0"),sQuery(id+"F0.wireOp",EDGE,"E4.0.14.0"),sQuery(id+"F0.wireOp",EDGE,"E4.3.14.0"),sQuery(id+"F0.wireOp",EDGE,"E4.6.14.0"),sQuery(id+"F0.wireOp",EDGE,"E4.9.14.0"),sQuery(id+"F0.wireOp",EDGE,"E4.0.15.0"),sQuery(id+"F0.wireOp",EDGE,"E4.3.15.0"),sQuery(id+"F0.wireOp",EDGE,"E4.6.15.0"),sQuery(id+"F0.wireOp",EDGE,"E4.9.15.0"),sQuery(id+"F0.wireOp",EDGE,"E4.0.16.0"),sQuery(id+"F0.wireOp",EDGE,"E4.3.16.0"),sQuery(id+"F0.wireOp",EDGE,"E4.6.16.0"),sQuery(id+"F0.wireOp",EDGE,"E4.9.16.0"),sQuery(id+"F0.wireOp",EDGE,"E4.0.17.0"),sQuery(id+"F0.wireOp",EDGE,"E4.3.17.0"),sQuery(id+"F0.wireOp",EDGE,"E4.6.17.0"),sQuery(id+"F0.wireOp",EDGE,"E4.9.17.0"),sQuery(id+"F0.wireOp",EDGE,"E4.0.18.0"),sQuery(id+"F0.wireOp",EDGE,"E4.3.18.0"),sQuery(id+"F0.wireOp",EDGE,"E4.6.18.0"),sQuery(id+"F0.wireOp",EDGE,"E4.9.18.0"),sQuery(id+"F0.wireOp",EDGE,"E4.0.19.0"),sQuery(id+"F0.wireOp",EDGE,"E4.3.19.0"),sQuery(id+"F0.wireOp",EDGE,"E4.6.19.0"),sQuery(id+"F0.wireOp",EDGE,"E4.9.19.0"),sQuery(id+"F0.wireOp",EDGE,"E5.0.1.0"),sQuery(id+"F0.wireOp",EDGE,"E5.0.1.1"),sQuery(id+"F0.wireOp",EDGE,"E5.0.1.2"),sQuery(id+"F0.wireOp",EDGE,"E5.0.1.3"),sQuery(id+"F0.wireOp",EDGE,"E5.0.1.4"),sQuery(id+"F0.wireOp",EDGE,"E5.0.1.5"),sQuery(id+"F0.wireOp",EDGE,"E5.0.1.6"),sQuery(id+"F0.wireOp",EDGE,"E5.0.1.7"),sQuery(id+"F0.wireOp",EDGE,"E5.0.1.8"),sQuery(id+"F0.wireOp",EDGE,"E5.0.1.9"),sQuery(id+"F0.wireOp",EDGE,"E5.0.1.10"),sQuery(id+"F0.wireOp",EDGE,"E5.0.1.11"),sQuery(id+"F0.wireOp",EDGE,"E5.0.1.12"),sQuery(id+"F0.wireOp",EDGE,"E5.0.1.13"),sQuery(id+"F0.wireOp",EDGE,"E5.0.1.14"),sQuery(id+"F0.wireOp",EDGE,"E5.0.1.15"),sQuery(id+"F0.wireOp",EDGE,"E5.0.1.16"),sQuery(id+"F0.wireOp",EDGE,"E5.0.1.17"),sQuery(id+"F0.wireOp",EDGE,"E5.0.1.18"),sQuery(id+"F0.wireOp",EDGE,"E5.0.1.19"),sQuery(id+"F0.wireOp",EDGE,"E5.0.1.20"),sQuery(id+"F0.wireOp",EDGE,"E5.0.1.21"),sQuery(id+"F0.wireOp",EDGE,"E5.0.1.22"),sQuery(id+"F0.wireOp",EDGE,"E5.0.1.23"),sQuery(id+"F0.wireOp",EDGE,"E5.0.1.24"),sQuery(id+"F0.wireOp",EDGE,"E5.0.1.25"),sQuery(id+"F0.wireOp",EDGE,"E5.0.1.26"),sQuery(id+"F0.wireOp",EDGE,"E5.0.1.27"),sQuery(id+"F0.wireOp",EDGE,"E5.0.1.28"),sQuery(id+"F0.wireOp",EDGE,"E5.0.1.29"),sQuery(id+"F0.wireOp",EDGE,"E5.0.1.30"),sQuery(id+"F0.wireOp",EDGE,"E5.0.1.31"),sQuery(id+"F0.wireOp",EDGE,"E5.0.1.32"),sQuery(id+"F0.wireOp",EDGE,"E5.0.1.33"),sQuery(id+"F0.wireOp",EDGE,"E5.0.1.34"),sQuery(id+"F0.wireOp",EDGE,"E5.0.1.35"),sQuery(id+"F0.wireOp",EDGE,"E5.0.1.36"),sQuery(id+"F0.wireOp",EDGE,"E5.0.1.37"),sQuery(id+"F0.wireOp",EDGE,"E5.0.1.38"),sQuery(id+"F0.wireOp",EDGE,"E5.0.1.39"),sQuery(id+"F0.wireOp",EDGE,"E5.0.1.40"),sQuery(id+"F0.wireOp",EDGE,"E5.0.1.41"),sQuery(id+"F0.wireOp",EDGE,"E5.0.1.42"),sQuery(id+"F0.wireOp",EDGE,"E5.0.1.43"),sQuery(id+"F0.wireOp",EDGE,"E5.0.1.44"),sQuery(id+"F0.wireOp",EDGE,"E5.0.1.45"),sQuery(id+"F0.wireOp",EDGE,"E5.0.1.46"),sQuery(id+"F0.wireOp",EDGE,"E5.0.1.47"),sQuery(id+"F0.wireOp",EDGE,"E5.0.1.48"),sQuery(id+"F0.wireOp",EDGE,"E5.0.1.49"),sQuery(id+"F0.wireOp",EDGE,"E5.0.1.50"),sQuery(id+"F0.wireOp",EDGE,"E5.0.1.51"),sQuery(id+"F0.wireOp",EDGE,"E5.0.1.52"),sQuery(id+"F0.wireOp",EDGE,"E5.0.1.53"),sQuery(id+"F0.wireOp",EDGE,"E5.0.1.54"),sQuery(id+"F0.wireOp",EDGE,"E5.0.1.55"),sQuery(id+"F0.wireOp",EDGE,"E5.0.1.57"),sQuery(id+"F0.wireOp",EDGE,"E5.0.1.58"),sQuery(id+"F0.wireOp",EDGE,"E5.0.1.59"),sQuery(id+"F0.wireOp",EDGE,"E5.0.1.60"),sQuery(id+"F0.wireOp",EDGE,"E5.0.1.61"),sQuery(id+"F0.wireOp",EDGE,"E5.0.1.62"),sQuery(id+"F0.wireOp",EDGE,"E5.0.1.63"),sQuery(id+"F0.wireOp",EDGE,"E5.0.1.64"),sQuery(id+"F0.wireOp",EDGE,"E5.0.1.65"),sQuery(id+"F0.wireOp",EDGE,"E5.0.1.66"),sQuery(id+"F0.wireOp",EDGE,"E5.0.1.67"),sQuery(id+"F0.wireOp",EDGE,"E5.0.1.68"),sQuery(id+"F0.wireOp",EDGE,"E5.0.1.69"),sQuery(id+"F0.wireOp",EDGE,"E5.0.1.70"),sQuery(id+"F0.wireOp",EDGE,"E5.0.1.71"),sQuery(id+"F0.wireOp",EDGE,"E5.0.1.72"),sQuery(id+"F0.wireOp",EDGE,"E5.0.1.73"),sQuery(id+"F0.wireOp",EDGE,"E5.0.1.74"),sQuery(id+"F0.wireOp",EDGE,"E5.0.1.75"),sQuery(id+"F0.wireOp",EDGE,"E5.0.1.76"),sQuery(id+"F0.wireOp",EDGE,"E5.0.1.77"),sQuery(id+"F0.wireOp",EDGE,"E5.0.1.78"),sQuery(id+"F0.wireOp",EDGE,"E5.0.1.79"),sQuery(id+"F0.wireOp",EDGE,"E5.0.1.80"),sQuery(id+"F0.wireOp",EDGE,"E5.0.2.0"),sQuery(id+"F0.wireOp",EDGE,"E5.0.2.1"),sQuery(id+"F0.wireOp",EDGE,"E5.0.2.2"),sQuery(id+"F0.wireOp",EDGE,"E5.0.2.3"),sQuery(id+"F0.wireOp",EDGE,"E5.0.2.4"),sQuery(id+"F0.wireOp",EDGE,"E5.0.2.5"),sQuery(id+"F0.wireOp",EDGE,"E5.0.2.6"),sQuery(id+"F0.wireOp",EDGE,"E5.0.2.7"),sQuery(id+"F0.wireOp",EDGE,"E5.0.2.8"),sQuery(id+"F0.wireOp",EDGE,"E5.0.2.9"),sQuery(id+"F0.wireOp",EDGE,"E5.0.2.10"),sQuery(id+"F0.wireOp",EDGE,"E5.0.2.11"),sQuery(id+"F0.wireOp",EDGE,"E5.0.2.12"),sQuery(id+"F0.wireOp",EDGE,"E5.0.2.13"),sQuery(id+"F0.wireOp",EDGE,"E5.0.2.14"),sQuery(id+"F0.wireOp",EDGE,"E5.0.2.15"),sQuery(id+"F0.wireOp",EDGE,"E5.0.2.16"),sQuery(id+"F0.wireOp",EDGE,"E5.0.2.17"),sQuery(id+"F0.wireOp",EDGE,"E5.0.2.18"),sQuery(id+"F0.wireOp",EDGE,"E5.0.2.19"),sQuery(id+"F0.wireOp",EDGE,"E5.0.2.20"),sQuery(id+"F0.wireOp",EDGE,"E5.0.2.21"),sQuery(id+"F0.wireOp",EDGE,"E5.0.2.22"),sQuery(id+"F0.wireOp",EDGE,"E5.0.2.23"),sQuery(id+"F0.wireOp",EDGE,"E5.0.2.24"),sQuery(id+"F0.wireOp",EDGE,"E5.0.2.25"),sQuery(id+"F0.wireOp",EDGE,"E5.0.2.26"),sQuery(id+"F0.wireOp",EDGE,"E5.0.2.27"),sQuery(id+"F0.wireOp",EDGE,"E5.0.2.28"),sQuery(id+"F0.wireOp",EDGE,"E5.0.2.29"),sQuery(id+"F0.wireOp",EDGE,"E5.0.2.30"),sQuery(id+"F0.wireOp",EDGE,"E5.0.2.31"),sQuery(id+"F0.wireOp",EDGE,"E5.0.2.32"),sQuery(id+"F0.wireOp",EDGE,"E5.0.2.33"),sQuery(id+"F0.wireOp",EDGE,"E5.0.2.34"),sQuery(id+"F0.wireOp",EDGE,"E5.0.2.35"),sQuery(id+"F0.wireOp",EDGE,"E5.0.2.36"),sQuery(id+"F0.wireOp",EDGE,"E5.0.2.37"),sQuery(id+"F0.wireOp",EDGE,"E5.0.2.38"),sQuery(id+"F0.wireOp",EDGE,"E5.0.2.39"),sQuery(id+"F0.wireOp",EDGE,"E5.0.2.40"),sQuery(id+"F0.wireOp",EDGE,"E5.0.2.41"),sQuery(id+"F0.wireOp",EDGE,"E5.0.2.42"),sQuery(id+"F0.wireOp",EDGE,"E5.0.2.43"),sQuery(id+"F0.wireOp",EDGE,"E5.0.2.44"),sQuery(id+"F0.wireOp",EDGE,"E5.0.2.45"),sQuery(id+"F0.wireOp",EDGE,"E5.0.2.46"),sQuery(id+"F0.wireOp",EDGE,"E5.0.2.47"),sQuery(id+"F0.wireOp",EDGE,"E5.0.2.48"),sQuery(id+"F0.wireOp",EDGE,"E5.0.2.49"),sQuery(id+"F0.wireOp",EDGE,"E5.0.2.50"),sQuery(id+"F0.wireOp",EDGE,"E5.0.2.51"),sQuery(id+"F0.wireOp",EDGE,"E5.0.2.52"),sQuery(id+"F0.wireOp",EDGE,"E5.0.2.53"),sQuery(id+"F0.wireOp",EDGE,"E5.0.2.54"),sQuery(id+"F0.wireOp",EDGE,"E5.0.2.55"),sQuery(id+"F0.wireOp",EDGE,"E5.0.2.57"),sQuery(id+"F0.wireOp",EDGE,"E5.0.2.58"),sQuery(id+"F0.wireOp",EDGE,"E5.0.2.59"),sQuery(id+"F0.wireOp",EDGE,"E5.0.2.60"),sQuery(id+"F0.wireOp",EDGE,"E5.0.2.61"),sQuery(id+"F0.wireOp",EDGE,"E5.0.2.62"),sQuery(id+"F0.wireOp",EDGE,"E5.0.2.63"),sQuery(id+"F0.wireOp",EDGE,"E5.0.2.64"),sQuery(id+"F0.wireOp",EDGE,"E5.0.2.65"),sQuery(id+"F0.wireOp",EDGE,"E5.0.2.66"),sQuery(id+"F0.wireOp",EDGE,"E5.0.2.67"),sQuery(id+"F0.wireOp",EDGE,"E5.0.2.68"),sQuery(id+"F0.wireOp",EDGE,"E5.0.2.69"),sQuery(id+"F0.wireOp",EDGE,"E5.0.2.70"),sQuery(id+"F0.wireOp",EDGE,"E5.0.2.71"),sQuery(id+"F0.wireOp",EDGE,"E5.0.2.72"),sQuery(id+"F0.wireOp",EDGE,"E5.0.2.73"),sQuery(id+"F0.wireOp",EDGE,"E5.0.2.74"),sQuery(id+"F0.wireOp",EDGE,"E5.0.2.75"),sQuery(id+"F0.wireOp",EDGE,"E5.0.2.76"),sQuery(id+"F0.wireOp",EDGE,"E5.0.2.77"),sQuery(id+"F0.wireOp",EDGE,"E5.0.2.78"),sQuery(id+"F0.wireOp",EDGE,"E5.0.2.79"),sQuery(id+"F0.wireOp",EDGE,"E5.0.2.80"),sQuery(id+"F0.wireOp",EDGE,"E5.0.3.0"),sQuery(id+"F0.wireOp",EDGE,"E5.0.3.1"),sQuery(id+"F0.wireOp",EDGE,"E5.0.3.2"),sQuery(id+"F0.wireOp",EDGE,"E5.0.3.3"),sQuery(id+"F0.wireOp",EDGE,"E5.0.3.4"),sQuery(id+"F0.wireOp",EDGE,"E5.0.3.5"),sQuery(id+"F0.wireOp",EDGE,"E5.0.3.6"),sQuery(id+"F0.wireOp",EDGE,"E5.0.3.7"),sQuery(id+"F0.wireOp",EDGE,"E5.0.3.8"),sQuery(id+"F0.wireOp",EDGE,"E5.0.3.9"),sQuery(id+"F0.wireOp",EDGE,"E5.0.3.10"),sQuery(id+"F0.wireOp",EDGE,"E5.0.3.11"),sQuery(id+"F0.wireOp",EDGE,"E5.0.3.12"),sQuery(id+"F0.wireOp",EDGE,"E5.0.3.13"),sQuery(id+"F0.wireOp",EDGE,"E5.0.3.14"),sQuery(id+"F0.wireOp",EDGE,"E5.0.3.15"),sQuery(id+"F0.wireOp",EDGE,"E5.0.3.16"),sQuery(id+"F0.wireOp",EDGE,"E5.0.3.17"),sQuery(id+"F0.wireOp",EDGE,"E5.0.3.18"),sQuery(id+"F0.wireOp",EDGE,"E5.0.3.19"),sQuery(id+"F0.wireOp",EDGE,"E5.0.3.20"),sQuery(id+"F0.wireOp",EDGE,"E5.0.3.21"),sQuery(id+"F0.wireOp",EDGE,"E5.0.3.22"),sQuery(id+"F0.wireOp",EDGE,"E5.0.3.23"),sQuery(id+"F0.wireOp",EDGE,"E5.0.3.24"),sQuery(id+"F0.wireOp",EDGE,"E5.0.3.25"),sQuery(id+"F0.wireOp",EDGE,"E5.0.3.26"),sQuery(id+"F0.wireOp",EDGE,"E5.0.3.27"),sQuery(id+"F0.wireOp",EDGE,"E5.0.3.28"),sQuery(id+"F0.wireOp",EDGE,"E5.0.3.29"),sQuery(id+"F0.wireOp",EDGE,"E5.0.3.30"),sQuery(id+"F0.wireOp",EDGE,"E5.0.3.31"),sQuery(id+"F0.wireOp",EDGE,"E5.0.3.32"),sQuery(id+"F0.wireOp",EDGE,"E5.0.3.33"),sQuery(id+"F0.wireOp",EDGE,"E5.0.3.34"),sQuery(id+"F0.wireOp",EDGE,"E5.0.3.35"),sQuery(id+"F0.wireOp",EDGE,"E5.0.3.36"),sQuery(id+"F0.wireOp",EDGE,"E5.0.3.37"),sQuery(id+"F0.wireOp",EDGE,"E5.0.3.38"),sQuery(id+"F0.wireOp",EDGE,"E5.0.3.39"),sQuery(id+"F0.wireOp",EDGE,"E5.0.3.40"),sQuery(id+"F0.wireOp",EDGE,"E5.0.3.41"),sQuery(id+"F0.wireOp",EDGE,"E5.0.3.42"),sQuery(id+"F0.wireOp",EDGE,"E5.0.3.43"),sQuery(id+"F0.wireOp",EDGE,"E5.0.3.44"),sQuery(id+"F0.wireOp",EDGE,"E5.0.3.45"),sQuery(id+"F0.wireOp",EDGE,"E5.0.3.46"),sQuery(id+"F0.wireOp",EDGE,"E5.0.3.47"),sQuery(id+"F0.wireOp",EDGE,"E5.0.3.48"),sQuery(id+"F0.wireOp",EDGE,"E5.0.3.49"),sQuery(id+"F0.wireOp",EDGE,"E5.0.3.50"),sQuery(id+"F0.wireOp",EDGE,"E5.0.3.51"),sQuery(id+"F0.wireOp",EDGE,"E5.0.3.52"),sQuery(id+"F0.wireOp",EDGE,"E5.0.3.53"),sQuery(id+"F0.wireOp",EDGE,"E5.0.3.54"),sQuery(id+"F0.wireOp",EDGE,"E5.0.3.55"),sQuery(id+"F0.wireOp",EDGE,"E5.0.3.57"),sQuery(id+"F0.wireOp",EDGE,"E5.0.3.58"),sQuery(id+"F0.wireOp",EDGE,"E5.0.3.59"),sQuery(id+"F0.wireOp",EDGE,"E5.0.3.60"),sQuery(id+"F0.wireOp",EDGE,"E5.0.3.61"),sQuery(id+"F0.wireOp",EDGE,"E5.0.3.62"),sQuery(id+"F0.wireOp",EDGE,"E5.0.3.63"),sQuery(id+"F0.wireOp",EDGE,"E5.0.3.64"),sQuery(id+"F0.wireOp",EDGE,"E5.0.3.65"),sQuery(id+"F0.wireOp",EDGE,"E5.0.3.66"),sQuery(id+"F0.wireOp",EDGE,"E5.0.3.67"),sQuery(id+"F0.wireOp",EDGE,"E5.0.3.68"),sQuery(id+"F0.wireOp",EDGE,"E5.0.3.69"),sQuery(id+"F0.wireOp",EDGE,"E5.0.3.70"),sQuery(id+"F0.wireOp",EDGE,"E5.0.3.71"),sQuery(id+"F0.wireOp",EDGE,"E5.0.3.72"),sQuery(id+"F0.wireOp",EDGE,"E5.0.3.73"),sQuery(id+"F0.wireOp",EDGE,"E5.0.3.74"),sQuery(id+"F0.wireOp",EDGE,"E5.0.3.75"),sQuery(id+"F0.wireOp",EDGE,"E5.0.3.76"),sQuery(id+"F0.wireOp",EDGE,"E5.0.3.77"),sQuery(id+"F0.wireOp",EDGE,"E5.0.3.78"),sQuery(id+"F0.wireOp",EDGE,"E5.0.3.79"),sQuery(id+"F0.wireOp",EDGE,"E5.0.3.80"),sQuery(id+"F0.wireOp",EDGE,"E5.0.4.0"),sQuery(id+"F0.wireOp",EDGE,"E5.0.4.1"),sQuery(id+"F0.wireOp",EDGE,"E5.0.4.2"),sQuery(id+"F0.wireOp",EDGE,"E5.0.4.3"),sQuery(id+"F0.wireOp",EDGE,"E5.0.4.4"),sQuery(id+"F0.wireOp",EDGE,"E5.0.4.5"),sQuery(id+"F0.wireOp",EDGE,"E5.0.4.6"),sQuery(id+"F0.wireOp",EDGE,"E5.0.4.7"),sQuery(id+"F0.wireOp",EDGE,"E5.0.4.8"),sQuery(id+"F0.wireOp",EDGE,"E5.0.4.9"),sQuery(id+"F0.wireOp",EDGE,"E5.0.4.10"),sQuery(id+"F0.wireOp",EDGE,"E5.0.4.11"),sQuery(id+"F0.wireOp",EDGE,"E5.0.4.12"),sQuery(id+"F0.wireOp",EDGE,"E5.0.4.13"),sQuery(id+"F0.wireOp",EDGE,"E5.0.4.14"),sQuery(id+"F0.wireOp",EDGE,"E5.0.4.15"),sQuery(id+"F0.wireOp",EDGE,"E5.0.4.16"),sQuery(id+"F0.wireOp",EDGE,"E5.0.4.17"),sQuery(id+"F0.wireOp",EDGE,"E5.0.4.18"),sQuery(id+"F0.wireOp",EDGE,"E5.0.4.19"),sQuery(id+"F0.wireOp",EDGE,"E5.0.4.20"),sQuery(id+"F0.wireOp",EDGE,"E5.0.4.21"),sQuery(id+"F0.wireOp",EDGE,"E5.0.4.22"),sQuery(id+"F0.wireOp",EDGE,"E5.0.4.23"),sQuery(id+"F0.wireOp",EDGE,"E5.0.4.24"),sQuery(id+"F0.wireOp",EDGE,"E5.0.4.25"),sQuery(id+"F0.wireOp",EDGE,"E5.0.4.26"),sQuery(id+"F0.wireOp",EDGE,"E5.0.4.27"),sQuery(id+"F0.wireOp",EDGE,"E5.0.4.28"),sQuery(id+"F0.wireOp",EDGE,"E5.0.4.29"),sQuery(id+"F0.wireOp",EDGE,"E5.0.4.30"),sQuery(id+"F0.wireOp",EDGE,"E5.0.4.31"),sQuery(id+"F0.wireOp",EDGE,"E5.0.4.32"),sQuery(id+"F0.wireOp",EDGE,"E5.0.4.33"),sQuery(id+"F0.wireOp",EDGE,"E5.0.4.34"),sQuery(id+"F0.wireOp",EDGE,"E5.0.4.35"),sQuery(id+"F0.wireOp",EDGE,"E5.0.4.36"),sQuery(id+"F0.wireOp",EDGE,"E5.0.4.37"),sQuery(id+"F0.wireOp",EDGE,"E5.0.4.38"),sQuery(id+"F0.wireOp",EDGE,"E5.0.4.39"),sQuery(id+"F0.wireOp",EDGE,"E5.0.4.40"),sQuery(id+"F0.wireOp",EDGE,"E5.0.4.41"),sQuery(id+"F0.wireOp",EDGE,"E5.0.4.42"),sQuery(id+"F0.wireOp",EDGE,"E5.0.4.43"),sQuery(id+"F0.wireOp",EDGE,"E5.0.4.44"),sQuery(id+"F0.wireOp",EDGE,"E5.0.4.45"),sQuery(id+"F0.wireOp",EDGE,"E5.0.4.46"),sQuery(id+"F0.wireOp",EDGE,"E5.0.4.47"),sQuery(id+"F0.wireOp",EDGE,"E5.0.4.48"),sQuery(id+"F0.wireOp",EDGE,"E5.0.4.49"),sQuery(id+"F0.wireOp",EDGE,"E5.0.4.50"),sQuery(id+"F0.wireOp",EDGE,"E5.0.4.51"),sQuery(id+"F0.wireOp",EDGE,"E5.0.4.52"),sQuery(id+"F0.wireOp",EDGE,"E5.0.4.53"),sQuery(id+"F0.wireOp",EDGE,"E5.0.4.54"),sQuery(id+"F0.wireOp",EDGE,"E5.0.4.55"),sQuery(id+"F0.wireOp",EDGE,"E5.0.4.57"),sQuery(id+"F0.wireOp",EDGE,"E5.0.4.58"),sQuery(id+"F0.wireOp",EDGE,"E5.0.4.59"),sQuery(id+"F0.wireOp",EDGE,"E5.0.4.60"),sQuery(id+"F0.wireOp",EDGE,"E5.0.4.61"),sQuery(id+"F0.wireOp",EDGE,"E5.0.4.62"),sQuery(id+"F0.wireOp",EDGE,"E5.0.4.63"),sQuery(id+"F0.wireOp",EDGE,"E5.0.4.64"),sQuery(id+"F0.wireOp",EDGE,"E5.0.4.65"),sQuery(id+"F0.wireOp",EDGE,"E5.0.4.66"),sQuery(id+"F0.wireOp",EDGE,"E5.0.4.67"),sQuery(id+"F0.wireOp",EDGE,"E5.0.4.68"),sQuery(id+"F0.wireOp",EDGE,"E5.0.4.69"),sQuery(id+"F0.wireOp",EDGE,"E5.0.4.70"),sQuery(id+"F0.wireOp",EDGE,"E5.0.4.71"),sQuery(id+"F0.wireOp",EDGE,"E5.0.4.72"),sQuery(id+"F0.wireOp",EDGE,"E5.0.4.73"),sQuery(id+"F0.wireOp",EDGE,"E5.0.4.74"),sQuery(id+"F0.wireOp",EDGE,"E5.0.4.75"),sQuery(id+"F0.wireOp",EDGE,"E5.0.4.76"),sQuery(id+"F0.wireOp",EDGE,"E5.0.4.77"),sQuery(id+"F0.wireOp",EDGE,"E5.0.4.78"),sQuery(id+"F0.wireOp",EDGE,"E5.0.4.79"),sQuery(id+"F0.wireOp",EDGE,"E5.0.4.80"),sQuery(id+"F0.wireOp",EDGE,"E5.0.5.0"),sQuery(id+"F0.wireOp",EDGE,"E5.0.5.1"),sQuery(id+"F0.wireOp",EDGE,"E5.0.5.2"),sQuery(id+"F0.wireOp",EDGE,"E5.0.5.3"),sQuery(id+"F0.wireOp",EDGE,"E5.0.5.4"),sQuery(id+"F0.wireOp",EDGE,"E5.0.5.5"),sQuery(id+"F0.wireOp",EDGE,"E5.0.5.6"),sQuery(id+"F0.wireOp",EDGE,"E5.0.5.7"),sQuery(id+"F0.wireOp",EDGE,"E5.0.5.8"),sQuery(id+"F0.wireOp",EDGE,"E5.0.5.9"),sQuery(id+"F0.wireOp",EDGE,"E5.0.5.10"),sQuery(id+"F0.wireOp",EDGE,"E5.0.5.11"),sQuery(id+"F0.wireOp",EDGE,"E5.0.5.12"),sQuery(id+"F0.wireOp",EDGE,"E5.0.5.13"),sQuery(id+"F0.wireOp",EDGE,"E5.0.5.14"),sQuery(id+"F0.wireOp",EDGE,"E5.0.5.15"),sQuery(id+"F0.wireOp",EDGE,"E5.0.5.16"),sQuery(id+"F0.wireOp",EDGE,"E5.0.5.17"),sQuery(id+"F0.wireOp",EDGE,"E5.0.5.18"),sQuery(id+"F0.wireOp",EDGE,"E5.0.5.19"),sQuery(id+"F0.wireOp",EDGE,"E5.0.5.20"),sQuery(id+"F0.wireOp",EDGE,"E5.0.5.21"),sQuery(id+"F0.wireOp",EDGE,"E5.0.5.22"),sQuery(id+"F0.wireOp",EDGE,"E5.0.5.23"),sQuery(id+"F0.wireOp",EDGE,"E5.0.5.24"),sQuery(id+"F0.wireOp",EDGE,"E5.0.5.25"),sQuery(id+"F0.wireOp",EDGE,"E5.0.5.26"),sQuery(id+"F0.wireOp",EDGE,"E5.0.5.27"),sQuery(id+"F0.wireOp",EDGE,"E5.0.5.28"),sQuery(id+"F0.wireOp",EDGE,"E5.0.5.29"),sQuery(id+"F0.wireOp",EDGE,"E5.0.5.30"),sQuery(id+"F0.wireOp",EDGE,"E5.0.5.31"),sQuery(id+"F0.wireOp",EDGE,"E5.0.5.32"),sQuery(id+"F0.wireOp",EDGE,"E5.0.5.33"),sQuery(id+"F0.wireOp",EDGE,"E5.0.5.34"),sQuery(id+"F0.wireOp",EDGE,"E5.0.5.35"),sQuery(id+"F0.wireOp",EDGE,"E5.0.5.36"),sQuery(id+"F0.wireOp",EDGE,"E5.0.5.37"),sQuery(id+"F0.wireOp",EDGE,"E5.0.5.38"),sQuery(id+"F0.wireOp",EDGE,"E5.0.5.39"),sQuery(id+"F0.wireOp",EDGE,"E5.0.5.40"),sQuery(id+"F0.wireOp",EDGE,"E5.0.5.41"),sQuery(id+"F0.wireOp",EDGE,"E5.0.5.42"),sQuery(id+"F0.wireOp",EDGE,"E5.0.5.43"),sQuery(id+"F0.wireOp",EDGE,"E5.0.5.44"),sQuery(id+"F0.wireOp",EDGE,"E5.0.5.45"),sQuery(id+"F0.wireOp",EDGE,"E5.0.5.46"),sQuery(id+"F0.wireOp",EDGE,"E5.0.5.47"),sQuery(id+"F0.wireOp",EDGE,"E5.0.5.48"),sQuery(id+"F0.wireOp",EDGE,"E5.0.5.49"),sQuery(id+"F0.wireOp",EDGE,"E5.0.5.50"),sQuery(id+"F0.wireOp",EDGE,"E5.0.5.51"),sQuery(id+"F0.wireOp",EDGE,"E5.0.5.52"),sQuery(id+"F0.wireOp",EDGE,"E5.0.5.53"),sQuery(id+"F0.wireOp",EDGE,"E5.0.5.54"),sQuery(id+"F0.wireOp",EDGE,"E5.0.5.55"),sQuery(id+"F0.wireOp",EDGE,"E5.0.5.57"),sQuery(id+"F0.wireOp",EDGE,"E5.0.5.58"),sQuery(id+"F0.wireOp",EDGE,"E5.0.5.59"),sQuery(id+"F0.wireOp",EDGE,"E5.0.5.60"),sQuery(id+"F0.wireOp",EDGE,"E5.0.5.61"),sQuery(id+"F0.wireOp",EDGE,"E5.0.5.62"),sQuery(id+"F0.wireOp",EDGE,"E5.0.5.63"),sQuery(id+"F0.wireOp",EDGE,"E5.0.5.64"),sQuery(id+"F0.wireOp",EDGE,"E5.0.5.65"),sQuery(id+"F0.wireOp",EDGE,"E5.0.5.66"),sQuery(id+"F0.wireOp",EDGE,"E5.0.5.67"),sQuery(id+"F0.wireOp",EDGE,"E5.0.5.68"),sQuery(id+"F0.wireOp",EDGE,"E5.0.5.69"),sQuery(id+"F0.wireOp",EDGE,"E5.0.5.70"),sQuery(id+"F0.wireOp",EDGE,"E5.0.5.71"),sQuery(id+"F0.wireOp",EDGE,"E5.0.5.72"),sQuery(id+"F0.wireOp",EDGE,"E5.0.5.73"),sQuery(id+"F0.wireOp",EDGE,"E5.0.5.74"),sQuery(id+"F0.wireOp",EDGE,"E5.0.5.75"),sQuery(id+"F0.wireOp",EDGE,"E5.0.5.76"),sQuery(id+"F0.wireOp",EDGE,"E5.0.5.77"),sQuery(id+"F0.wireOp",EDGE,"E5.0.5.78"),sQuery(id+"F0.wireOp",EDGE,"E5.0.5.79"),sQuery(id+"F0.wireOp",EDGE,"E5.0.5.80"),sQuery(id+"F0.wireOp",EDGE,"E5.0.6.0"),sQuery(id+"F0.wireOp",EDGE,"E5.0.6.1"),sQuery(id+"F0.wireOp",EDGE,"E5.0.6.2"),sQuery(id+"F0.wireOp",EDGE,"E5.0.6.3"),sQuery(id+"F0.wireOp",EDGE,"E5.0.6.4"),sQuery(id+"F0.wireOp",EDGE,"E5.0.6.5"),sQuery(id+"F0.wireOp",EDGE,"E5.0.6.6"),sQuery(id+"F0.wireOp",EDGE,"E5.0.6.7"),sQuery(id+"F0.wireOp",EDGE,"E5.0.6.8"),sQuery(id+"F0.wireOp",EDGE,"E5.0.6.9"),sQuery(id+"F0.wireOp",EDGE,"E5.0.6.10"),sQuery(id+"F0.wireOp",EDGE,"E5.0.6.11"),sQuery(id+"F0.wireOp",EDGE,"E5.0.6.12"),sQuery(id+"F0.wireOp",EDGE,"E5.0.6.13"),sQuery(id+"F0.wireOp",EDGE,"E5.0.6.14"),sQuery(id+"F0.wireOp",EDGE,"E5.0.6.15"),sQuery(id+"F0.wireOp",EDGE,"E5.0.6.16"),sQuery(id+"F0.wireOp",EDGE,"E5.0.6.17"),sQuery(id+"F0.wireOp",EDGE,"E5.0.6.18"),sQuery(id+"F0.wireOp",EDGE,"E5.0.6.19"),sQuery(id+"F0.wireOp",EDGE,"E5.0.6.20"),sQuery(id+"F0.wireOp",EDGE,"E5.0.6.21"),sQuery(id+"F0.wireOp",EDGE,"E5.0.6.22"),sQuery(id+"F0.wireOp",EDGE,"E5.0.6.23"),sQuery(id+"F0.wireOp",EDGE,"E5.0.6.24"),sQuery(id+"F0.wireOp",EDGE,"E5.0.6.25"),sQuery(id+"F0.wireOp",EDGE,"E5.0.6.26"),sQuery(id+"F0.wireOp",EDGE,"E5.0.6.27"),sQuery(id+"F0.wireOp",EDGE,"E5.0.6.28"),sQuery(id+"F0.wireOp",EDGE,"E5.0.6.29"),sQuery(id+"F0.wireOp",EDGE,"E5.0.6.30"),sQuery(id+"F0.wireOp",EDGE,"E5.0.6.31"),sQuery(id+"F0.wireOp",EDGE,"E5.0.6.32"),sQuery(id+"F0.wireOp",EDGE,"E5.0.6.33"),sQuery(id+"F0.wireOp",EDGE,"E5.0.6.34"),sQuery(id+"F0.wireOp",EDGE,"E5.0.6.35"),sQuery(id+"F0.wireOp",EDGE,"E5.0.6.36"),sQuery(id+"F0.wireOp",EDGE,"E5.0.6.37"),sQuery(id+"F0.wireOp",EDGE,"E5.0.6.38"),sQuery(id+"F0.wireOp",EDGE,"E5.0.6.39"),sQuery(id+"F0.wireOp",EDGE,"E5.0.6.40"),sQuery(id+"F0.wireOp",EDGE,"E5.0.6.41"),sQuery(id+"F0.wireOp",EDGE,"E5.0.6.42"),sQuery(id+"F0.wireOp",EDGE,"E5.0.6.43"),sQuery(id+"F0.wireOp",EDGE,"E5.0.6.44"),sQuery(id+"F0.wireOp",EDGE,"E5.0.6.45"),sQuery(id+"F0.wireOp",EDGE,"E5.0.6.46"),sQuery(id+"F0.wireOp",EDGE,"E5.0.6.47"),sQuery(id+"F0.wireOp",EDGE,"E5.0.6.48"),sQuery(id+"F0.wireOp",EDGE,"E5.0.6.49"),sQuery(id+"F0.wireOp",EDGE,"E5.0.6.50"),sQuery(id+"F0.wireOp",EDGE,"E5.0.6.51"),sQuery(id+"F0.wireOp",EDGE,"E5.0.6.52"),sQuery(id+"F0.wireOp",EDGE,"E5.0.6.53"),sQuery(id+"F0.wireOp",EDGE,"E5.0.6.54"),sQuery(id+"F0.wireOp",EDGE,"E5.0.6.55"),sQuery(id+"F0.wireOp",EDGE,"E5.0.6.57"),sQuery(id+"F0.wireOp",EDGE,"E5.0.6.58"),sQuery(id+"F0.wireOp",EDGE,"E5.0.6.59"),sQuery(id+"F0.wireOp",EDGE,"E5.0.6.60"),sQuery(id+"F0.wireOp",EDGE,"E5.0.6.61"),sQuery(id+"F0.wireOp",EDGE,"E5.0.6.62"),sQuery(id+"F0.wireOp",EDGE,"E5.0.6.63"),sQuery(id+"F0.wireOp",EDGE,"E5.0.6.64"),sQuery(id+"F0.wireOp",EDGE,"E5.0.6.65"),sQuery(id+"F0.wireOp",EDGE,"E5.0.6.66"),sQuery(id+"F0.wireOp",EDGE,"E5.0.6.67"),sQuery(id+"F0.wireOp",EDGE,"E5.0.6.68"),sQuery(id+"F0.wireOp",EDGE,"E5.0.6.69"),sQuery(id+"F0.wireOp",EDGE,"E5.0.6.70"),sQuery(id+"F0.wireOp",EDGE,"E5.0.6.71"),sQuery(id+"F0.wireOp",EDGE,"E5.0.6.72"),sQuery(id+"F0.wireOp",EDGE,"E5.0.6.73"),sQuery(id+"F0.wireOp",EDGE,"E5.0.6.74"),sQuery(id+"F0.wireOp",EDGE,"E5.0.6.75"),sQuery(id+"F0.wireOp",EDGE,"E5.0.6.76"),sQuery(id+"F0.wireOp",EDGE,"E5.0.6.77"),sQuery(id+"F0.wireOp",EDGE,"E5.0.6.78"),sQuery(id+"F0.wireOp",EDGE,"E5.0.6.79"),sQuery(id+"F0.wireOp",EDGE,"E5.0.6.80"),sQuery(id+"F0.wireOp",EDGE,"E5.0.7.0"),sQuery(id+"F0.wireOp",EDGE,"E5.0.7.1"),sQuery(id+"F0.wireOp",EDGE,"E5.0.7.2"),sQuery(id+"F0.wireOp",EDGE,"E5.0.7.3"),sQuery(id+"F0.wireOp",EDGE,"E5.0.7.4"),sQuery(id+"F0.wireOp",EDGE,"E5.0.7.5"),sQuery(id+"F0.wireOp",EDGE,"E5.0.7.6"),sQuery(id+"F0.wireOp",EDGE,"E5.0.7.7"),sQuery(id+"F0.wireOp",EDGE,"E5.0.7.8"),sQuery(id+"F0.wireOp",EDGE,"E5.0.7.9"),sQuery(id+"F0.wireOp",EDGE,"E5.0.7.10"),sQuery(id+"F0.wireOp",EDGE,"E5.0.7.11"),sQuery(id+"F0.wireOp",EDGE,"E5.0.7.12"),sQuery(id+"F0.wireOp",EDGE,"E5.0.7.13"),sQuery(id+"F0.wireOp",EDGE,"E5.0.7.14"),sQuery(id+"F0.wireOp",EDGE,"E5.0.7.15"),sQuery(id+"F0.wireOp",EDGE,"E5.0.7.16"),sQuery(id+"F0.wireOp",EDGE,"E5.0.7.17"),sQuery(id+"F0.wireOp",EDGE,"E5.0.7.18"),sQuery(id+"F0.wireOp",EDGE,"E5.0.7.19"),sQuery(id+"F0.wireOp",EDGE,"E5.0.7.20"),sQuery(id+"F0.wireOp",EDGE,"E5.0.7.21"),sQuery(id+"F0.wireOp",EDGE,"E5.0.7.22"),sQuery(id+"F0.wireOp",EDGE,"E5.0.7.23"),sQuery(id+"F0.wireOp",EDGE,"E5.0.7.24"),sQuery(id+"F0.wireOp",EDGE,"E5.0.7.25"),sQuery(id+"F0.wireOp",EDGE,"E5.0.7.26"),sQuery(id+"F0.wireOp",EDGE,"E5.0.7.27"),sQuery(id+"F0.wireOp",EDGE,"E5.0.7.28"),sQuery(id+"F0.wireOp",EDGE,"E5.0.7.29"),sQuery(id+"F0.wireOp",EDGE,"E5.0.7.30"),sQuery(id+"F0.wireOp",EDGE,"E5.0.7.31"),sQuery(id+"F0.wireOp",EDGE,"E5.0.7.32"),sQuery(id+"F0.wireOp",EDGE,"E5.0.7.33"),sQuery(id+"F0.wireOp",EDGE,"E5.0.7.34"),sQuery(id+"F0.wireOp",EDGE,"E5.0.7.35"),sQuery(id+"F0.wireOp",EDGE,"E5.0.7.36"),sQuery(id+"F0.wireOp",EDGE,"E5.0.7.37"),sQuery(id+"F0.wireOp",EDGE,"E5.0.7.38"),sQuery(id+"F0.wireOp",EDGE,"E5.0.7.39"),sQuery(id+"F0.wireOp",EDGE,"E5.0.7.40"),sQuery(id+"F0.wireOp",EDGE,"E5.0.7.41"),sQuery(id+"F0.wireOp",EDGE,"E5.0.7.42"),sQuery(id+"F0.wireOp",EDGE,"E5.0.7.43"),sQuery(id+"F0.wireOp",EDGE,"E5.0.7.44"),sQuery(id+"F0.wireOp",EDGE,"E5.0.7.45"),sQuery(id+"F0.wireOp",EDGE,"E5.0.7.46"),sQuery(id+"F0.wireOp",EDGE,"E5.0.7.47"),sQuery(id+"F0.wireOp",EDGE,"E5.0.7.48"),sQuery(id+"F0.wireOp",EDGE,"E5.0.7.49"),sQuery(id+"F0.wireOp",EDGE,"E5.0.7.50"),sQuery(id+"F0.wireOp",EDGE,"E5.0.7.51"),sQuery(id+"F0.wireOp",EDGE,"E5.0.7.52"),sQuery(id+"F0.wireOp",EDGE,"E5.0.7.53"),sQuery(id+"F0.wireOp",EDGE,"E5.0.7.54"),sQuery(id+"F0.wireOp",EDGE,"E5.0.7.55"),sQuery(id+"F0.wireOp",EDGE,"E5.0.7.57"),sQuery(id+"F0.wireOp",EDGE,"E5.0.7.58"),sQuery(id+"F0.wireOp",EDGE,"E5.0.7.59"),sQuery(id+"F0.wireOp",EDGE,"E5.0.7.60"),sQuery(id+"F0.wireOp",EDGE,"E5.0.7.61"),sQuery(id+"F0.wireOp",EDGE,"E5.0.7.62"),sQuery(id+"F0.wireOp",EDGE,"E5.0.7.63"),sQuery(id+"F0.wireOp",EDGE,"E5.0.7.64"),sQuery(id+"F0.wireOp",EDGE,"E5.0.7.65"),sQuery(id+"F0.wireOp",EDGE,"E5.0.7.66"),sQuery(id+"F0.wireOp",EDGE,"E5.0.7.67"),sQuery(id+"F0.wireOp",EDGE,"E5.0.7.68"),sQuery(id+"F0.wireOp",EDGE,"E5.0.7.69"),sQuery(id+"F0.wireOp",EDGE,"E5.0.7.70"),sQuery(id+"F0.wireOp",EDGE,"E5.0.7.71"),sQuery(id+"F0.wireOp",EDGE,"E5.0.7.72"),sQuery(id+"F0.wireOp",EDGE,"E5.0.7.73"),sQuery(id+"F0.wireOp",EDGE,"E5.0.7.74"),sQuery(id+"F0.wireOp",EDGE,"E5.0.7.75"),sQuery(id+"F0.wireOp",EDGE,"E5.0.7.76"),sQuery(id+"F0.wireOp",EDGE,"E5.0.7.77"),sQuery(id+"F0.wireOp",EDGE,"E5.0.7.78"),sQuery(id+"F0.wireOp",EDGE,"E5.0.7.79"),sQuery(id+"F0.wireOp",EDGE,"E5.0.7.80"),sQuery(id+"F0.wireOp",EDGE,"E5.0.8.0"),sQuery(id+"F0.wireOp",EDGE,"E5.0.8.1"),sQuery(id+"F0.wireOp",EDGE,"E5.0.8.2"),sQuery(id+"F0.wireOp",EDGE,"E5.0.8.3"),sQuery(id+"F0.wireOp",EDGE,"E5.0.8.4"),sQuery(id+"F0.wireOp",EDGE,"E5.0.8.5"),sQuery(id+"F0.wireOp",EDGE,"E5.0.8.6"),sQuery(id+"F0.wireOp",EDGE,"E5.0.8.7"),sQuery(id+"F0.wireOp",EDGE,"E5.0.8.8"),sQuery(id+"F0.wireOp",EDGE,"E5.0.8.9"),sQuery(id+"F0.wireOp",EDGE,"E5.0.8.10"),sQuery(id+"F0.wireOp",EDGE,"E5.0.8.11"),sQuery(id+"F0.wireOp",EDGE,"E5.0.8.12"),sQuery(id+"F0.wireOp",EDGE,"E5.0.8.13"),sQuery(id+"F0.wireOp",EDGE,"E5.0.8.14"),sQuery(id+"F0.wireOp",EDGE,"E5.0.8.15"),sQuery(id+"F0.wireOp",EDGE,"E5.0.8.16"),sQuery(id+"F0.wireOp",EDGE,"E5.0.8.17"),sQuery(id+"F0.wireOp",EDGE,"E5.0.8.18"),sQuery(id+"F0.wireOp",EDGE,"E5.0.8.19"),sQuery(id+"F0.wireOp",EDGE,"E5.0.8.20"),sQuery(id+"F0.wireOp",EDGE,"E5.0.8.21"),sQuery(id+"F0.wireOp",EDGE,"E5.0.8.22"),sQuery(id+"F0.wireOp",EDGE,"E5.0.8.23"),sQuery(id+"F0.wireOp",EDGE,"E5.0.8.24"),sQuery(id+"F0.wireOp",EDGE,"E5.0.8.25"),sQuery(id+"F0.wireOp",EDGE,"E5.0.8.26"),sQuery(id+"F0.wireOp",EDGE,"E5.0.8.27"),sQuery(id+"F0.wireOp",EDGE,"E5.0.8.28"),sQuery(id+"F0.wireOp",EDGE,"E5.0.8.29"),sQuery(id+"F0.wireOp",EDGE,"E5.0.8.30"),sQuery(id+"F0.wireOp",EDGE,"E5.0.8.31"),sQuery(id+"F0.wireOp",EDGE,"E5.0.8.32"),sQuery(id+"F0.wireOp",EDGE,"E5.0.8.33"),sQuery(id+"F0.wireOp",EDGE,"E5.0.8.34"),sQuery(id+"F0.wireOp",EDGE,"E5.0.8.35"),sQuery(id+"F0.wireOp",EDGE,"E5.0.8.36"),sQuery(id+"F0.wireOp",EDGE,"E5.0.8.37"),sQuery(id+"F0.wireOp",EDGE,"E5.0.8.38"),sQuery(id+"F0.wireOp",EDGE,"E5.0.8.39"),sQuery(id+"F0.wireOp",EDGE,"E5.0.8.40"),sQuery(id+"F0.wireOp",EDGE,"E5.0.8.41"),sQuery(id+"F0.wireOp",EDGE,"E5.0.8.42"),sQuery(id+"F0.wireOp",EDGE,"E5.0.8.43"),sQuery(id+"F0.wireOp",EDGE,"E5.0.8.44"),sQuery(id+"F0.wireOp",EDGE,"E5.0.8.45"),sQuery(id+"F0.wireOp",EDGE,"E5.0.8.46"),sQuery(id+"F0.wireOp",EDGE,"E5.0.8.47"),sQuery(id+"F0.wireOp",EDGE,"E5.0.8.48"),sQuery(id+"F0.wireOp",EDGE,"E5.0.8.49"),sQuery(id+"F0.wireOp",EDGE,"E5.0.8.50"),sQuery(id+"F0.wireOp",EDGE,"E5.0.8.51"),sQuery(id+"F0.wireOp",EDGE,"E5.0.8.52"),sQuery(id+"F0.wireOp",EDGE,"E5.0.8.53"),sQuery(id+"F0.wireOp",EDGE,"E5.0.8.54"),sQuery(id+"F0.wireOp",EDGE,"E5.0.8.55"),sQuery(id+"F0.wireOp",EDGE,"E5.0.8.57"),sQuery(id+"F0.wireOp",EDGE,"E5.0.8.58"),sQuery(id+"F0.wireOp",EDGE,"E5.0.8.59"),sQuery(id+"F0.wireOp",EDGE,"E5.0.8.60"),sQuery(id+"F0.wireOp",EDGE,"E5.0.8.61"),sQuery(id+"F0.wireOp",EDGE,"E5.0.8.62"),sQuery(id+"F0.wireOp",EDGE,"E5.0.8.63"),sQuery(id+"F0.wireOp",EDGE,"E5.0.8.64"),sQuery(id+"F0.wireOp",EDGE,"E5.0.8.65"),sQuery(id+"F0.wireOp",EDGE,"E5.0.8.66"),sQuery(id+"F0.wireOp",EDGE,"E5.0.8.67"),sQuery(id+"F0.wireOp",EDGE,"E5.0.8.68"),sQuery(id+"F0.wireOp",EDGE,"E5.0.8.69"),sQuery(id+"F0.wireOp",EDGE,"E5.0.8.70"),sQuery(id+"F0.wireOp",EDGE,"E5.0.8.71"),sQuery(id+"F0.wireOp",EDGE,"E5.0.8.72"),sQuery(id+"F0.wireOp",EDGE,"E5.0.8.73"),sQuery(id+"F0.wireOp",EDGE,"E5.0.8.74"),sQuery(id+"F0.wireOp",EDGE,"E5.0.8.75"),sQuery(id+"F0.wireOp",EDGE,"E5.0.8.76"),sQuery(id+"F0.wireOp",EDGE,"E5.0.8.77"),sQuery(id+"F0.wireOp",EDGE,"E5.0.8.78"),sQuery(id+"F0.wireOp",EDGE,"E5.0.8.79"),sQuery(id+"F0.wireOp",EDGE,"E5.0.8.80"),sQuery(id+"F0.wireOp",EDGE,"E5.0.9.0"),sQuery(id+"F0.wireOp",EDGE,"E5.0.9.1"),sQuery(id+"F0.wireOp",EDGE,"E5.0.9.2"),sQuery(id+"F0.wireOp",EDGE,"E5.0.9.3"),sQuery(id+"F0.wireOp",EDGE,"E5.0.9.4"),sQuery(id+"F0.wireOp",EDGE,"E5.0.9.5"),sQuery(id+"F0.wireOp",EDGE,"E5.0.9.6"),sQuery(id+"F0.wireOp",EDGE,"E5.0.9.7"),sQuery(id+"F0.wireOp",EDGE,"E5.0.9.8"),sQuery(id+"F0.wireOp",EDGE,"E5.0.9.9"),sQuery(id+"F0.wireOp",EDGE,"E5.0.9.10"),sQuery(id+"F0.wireOp",EDGE,"E5.0.9.11"),sQuery(id+"F0.wireOp",EDGE,"E5.0.9.12"),sQuery(id+"F0.wireOp",EDGE,"E5.0.9.13"),sQuery(id+"F0.wireOp",EDGE,"E5.0.9.14"),sQuery(id+"F0.wireOp",EDGE,"E5.0.9.15"),sQuery(id+"F0.wireOp",EDGE,"E5.0.9.16"),sQuery(id+"F0.wireOp",EDGE,"E5.0.9.17"),sQuery(id+"F0.wireOp",EDGE,"E5.0.9.18"),sQuery(id+"F0.wireOp",EDGE,"E5.0.9.19"),sQuery(id+"F0.wireOp",EDGE,"E5.0.9.20"),sQuery(id+"F0.wireOp",EDGE,"E5.0.9.21"),sQuery(id+"F0.wireOp",EDGE,"E5.0.9.22"),sQuery(id+"F0.wireOp",EDGE,"E5.0.9.23"),sQuery(id+"F0.wireOp",EDGE,"E5.0.9.24"),sQuery(id+"F0.wireOp",EDGE,"E5.0.9.25"),sQuery(id+"F0.wireOp",EDGE,"E5.0.9.26"),sQuery(id+"F0.wireOp",EDGE,"E5.0.9.27"),sQuery(id+"F0.wireOp",EDGE,"E5.0.9.28"),sQuery(id+"F0.wireOp",EDGE,"E5.0.9.29"),sQuery(id+"F0.wireOp",EDGE,"E5.0.9.30"),sQuery(id+"F0.wireOp",EDGE,"E5.0.9.31"),sQuery(id+"F0.wireOp",EDGE,"E5.0.9.32"),sQuery(id+"F0.wireOp",EDGE,"E5.0.9.33"),sQuery(id+"F0.wireOp",EDGE,"E5.0.9.34"),sQuery(id+"F0.wireOp",EDGE,"E5.0.9.35"),sQuery(id+"F0.wireOp",EDGE,"E5.0.9.36"),sQuery(id+"F0.wireOp",EDGE,"E5.0.9.37"),sQuery(id+"F0.wireOp",EDGE,"E5.0.9.38"),sQuery(id+"F0.wireOp",EDGE,"E5.0.9.39"),sQuery(id+"F0.wireOp",EDGE,"E5.0.9.40"),sQuery(id+"F0.wireOp",EDGE,"E5.0.9.41"),sQuery(id+"F0.wireOp",EDGE,"E5.0.9.42"),sQuery(id+"F0.wireOp",EDGE,"E5.0.9.43"),sQuery(id+"F0.wireOp",EDGE,"E5.0.9.44"),sQuery(id+"F0.wireOp",EDGE,"E5.0.9.45"),sQuery(id+"F0.wireOp",EDGE,"E5.0.9.46"),sQuery(id+"F0.wireOp",EDGE,"E5.0.9.47"),sQuery(id+"F0.wireOp",EDGE,"E5.0.9.48"),sQuery(id+"F0.wireOp",EDGE,"E5.0.9.49"),sQuery(id+"F0.wireOp",EDGE,"E5.0.9.50"),sQuery(id+"F0.wireOp",EDGE,"E5.0.9.51"),sQuery(id+"F0.wireOp",EDGE,"E5.0.9.52"),sQuery(id+"F0.wireOp",EDGE,"E5.0.9.53"),sQuery(id+"F0.wireOp",EDGE,"E5.0.9.54"),sQuery(id+"F0.wireOp",EDGE,"E5.0.9.55"),sQuery(id+"F0.wireOp",EDGE,"E5.0.9.57"),sQuery(id+"F0.wireOp",EDGE,"E5.0.9.58"),sQuery(id+"F0.wireOp",EDGE,"E5.0.9.59"),sQuery(id+"F0.wireOp",EDGE,"E5.0.9.60"),sQuery(id+"F0.wireOp",EDGE,"E5.0.9.61"),sQuery(id+"F0.wireOp",EDGE,"E5.0.9.62"),sQuery(id+"F0.wireOp",EDGE,"E5.0.9.63"),sQuery(id+"F0.wireOp",EDGE,"E5.0.9.64"),sQuery(id+"F0.wireOp",EDGE,"E5.0.9.65"),sQuery(id+"F0.wireOp",EDGE,"E5.0.9.66"),sQuery(id+"F0.wireOp",EDGE,"E5.0.9.67"),sQuery(id+"F0.wireOp",EDGE,"E5.0.9.68"),sQuery(id+"F0.wireOp",EDGE,"E5.0.9.69"),sQuery(id+"F0.wireOp",EDGE,"E5.0.9.70"),sQuery(id+"F0.wireOp",EDGE,"E5.0.9.71"),sQuery(id+"F0.wireOp",EDGE,"E5.0.9.72"),sQuery(id+"F0.wireOp",EDGE,"E5.0.9.73"),sQuery(id+"F0.wireOp",EDGE,"E5.0.9.74"),sQuery(id+"F0.wireOp",EDGE,"E5.0.9.75"),sQuery(id+"F0.wireOp",EDGE,"E5.0.9.76"),sQuery(id+"F0.wireOp",EDGE,"E5.0.9.77"),sQuery(id+"F0.wireOp",EDGE,"E5.0.9.78"),sQuery(id+"F0.wireOp",EDGE,"E5.0.9.79"),sQuery(id+"F0.wireOp",EDGE,"E5.0.9.80")])],"isStart":false});
            var sketch = newSketch(context, id + "F2", { "sketchPlane" : qUnion([Q0])});
            skLineSegment(sketch, "E6.bottom", {"start": v(-61.85, 33.34) * mm, "end": v(-58.67, 33.34) * mm});
            skLineSegment(sketch, "E6.top", {"start": v(-61.85, 30.16) * mm, "end": v(-58.67, 30.16) * mm});
            skLineSegment(sketch, "E6.left", {"start": v(-61.85, 33.34) * mm, "end": v(-61.85, 30.16) * mm});
            skLineSegment(sketch, "E6.right", {"start": v(-58.67, 33.34) * mm, "end": v(-58.67, 30.16) * mm});
            skLineSegment(sketch, "E7.bottom", {"start": v(63.5, 33.34) * mm, "end": v(60.32, 33.34) * mm});
            skLineSegment(sketch, "E7.top", {"start": v(63.5, 30.16) * mm, "end": v(60.32, 30.16) * mm});
            skLineSegment(sketch, "E7.left", {"start": v(63.5, 33.34) * mm, "end": v(63.5, 30.16) * mm});
            skLineSegment(sketch, "E7.right", {"start": v(60.32, 33.34) * mm, "end": v(60.32, 30.16) * mm});
            skLineSegment(sketch, "E8.bottom", {"start": v(63.5, -31.05) * mm, "end": v(60.32, -31.05) * mm});
            skLineSegment(sketch, "E8.top", {"start": v(63.5, -27.88) * mm, "end": v(60.32, -27.88) * mm});
            skLineSegment(sketch, "E8.left", {"start": v(63.5, -31.05) * mm, "end": v(63.5, -27.88) * mm});
            skLineSegment(sketch, "E8.right", {"start": v(60.32, -31.05) * mm, "end": v(60.32, -27.88) * mm});
            skLineSegment(sketch, "E9.bottom", {"start": v(-61.85, -31.05) * mm, "end": v(-58.67, -31.05) * mm});
            skLineSegment(sketch, "E9.top", {"start": v(-61.85, -27.88) * mm, "end": v(-58.67, -27.88) * mm});
            skLineSegment(sketch, "E9.left", {"start": v(-61.85, -31.05) * mm, "end": v(-61.85, -27.88) * mm});
            skLineSegment(sketch, "E9.right", {"start": v(-58.67, -31.05) * mm, "end": v(-58.67, -27.88) * mm});
            skLineSegment(sketch, "E10.bottom", {"start": v(-0.63, 30.16) * mm, "end": v(2.29, 30.16) * mm});
            skLineSegment(sketch, "E10.top", {"start": v(-0.63, 33.34) * mm, "end": v(2.29, 33.34) * mm});
            skLineSegment(sketch, "E10.left", {"start": v(-0.63, 30.16) * mm, "end": v(-0.63, 33.34) * mm});
            skLineSegment(sketch, "E10.right", {"start": v(2.29, 30.16) * mm, "end": v(2.29, 33.34) * mm});
            skLineSegment(sketch, "E11.bottom", {"start": v(-0.63, -27.88) * mm, "end": v(2.29, -27.88) * mm});
            skLineSegment(sketch, "E11.top", {"start": v(-0.63, -31.05) * mm, "end": v(2.29, -31.05) * mm});
            skLineSegment(sketch, "E11.left", {"start": v(-0.63, -27.88) * mm, "end": v(-0.63, -31.05) * mm});
            skLineSegment(sketch, "E11.right", {"start": v(2.29, -27.88) * mm, "end": v(2.29, -31.05) * mm});
            skSolve(sketch);
        }
        {
            var Q0;
            Q0 = qSketchRegion(id + "F2", true);
            extrude(context, id + "F3", {"entities" : qUnion([Q0]), "operationType" : NewBodyOperationType.ADD, "depth" : 50.8 * mm});
        }
    });
